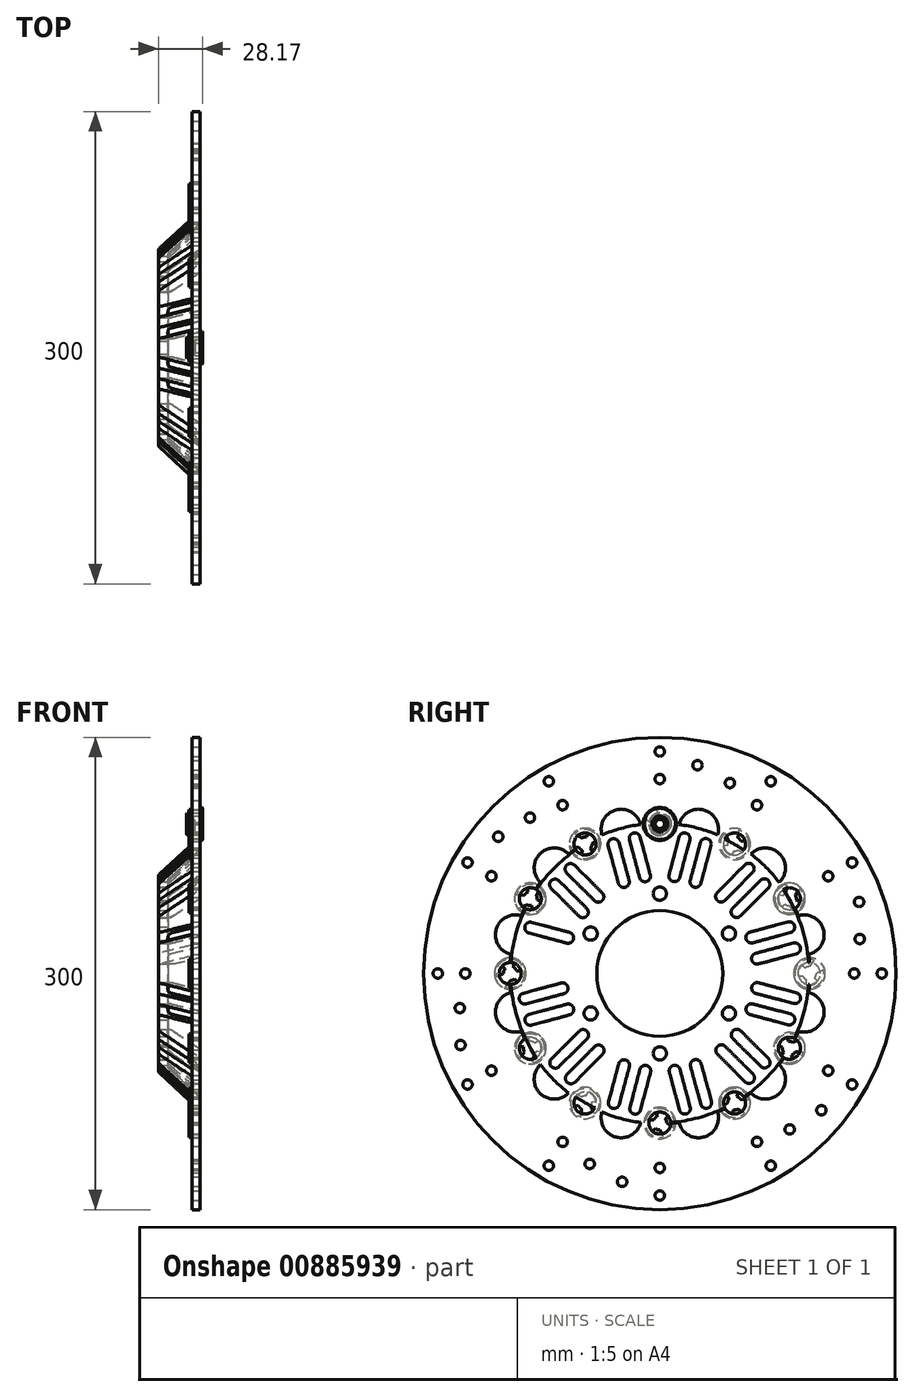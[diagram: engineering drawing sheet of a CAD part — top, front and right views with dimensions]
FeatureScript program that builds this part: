
annotation { "Feature Type Name" : "Feature", "Feature Type Description" : "" }
export const myFeature = defineFeature(function(context is Context, id is Id, definition is map)
    precondition{}
    {
        {
            var Q0;
            Q0=qCreatedBy(makeId("Front.planeOp"),FACE);
            var sketch = newSketch(context, id + "F0", { "sketchPlane" : qUnion([Q0])});
            skLineSegment(sketch, "E0", {"start": v(0, 79.9) * mm, "end": v(0, 150) * mm});
            skLineSegment(sketch, "E1", {"start": v(0, 150) * mm, "end": v(-5.08, 150) * mm});
            skLineSegment(sketch, "E2", {"start": v(-5.08, 150) * mm, "end": v(-5.08, 83.37) * mm});
            skLineSegment(sketch, "E3", {"start": v(-5.72, 81.9) * mm, "end": v(-25.96, 63.1) * mm});
            skLineSegment(sketch, "E4", {"start": v(-26.6, 61.63) * mm, "end": v(-26.6, 0) * mm});
            skLineSegment(sketch, "E5", {"start": v(-5.08, 82.5) * mm, "end": v(-5.08, 0) * mm, "construction": true});
            skLineSegment(sketch, "E6", {"start": v(-26.6, 0) * mm, "end": v(-20.6, 0) * mm});
            skLineSegment(sketch, "E7", {"start": v(-20.6, 0) * mm, "end": v(-20.6, 59.01) * mm});
            skLineSegment(sketch, "E8", {"start": v(-19.96, 60.48) * mm, "end": v(-0.64, 78.44) * mm});
            skPoint(sketch, "E9.visualSharp", {"position": v(-5.08, 82.5) * mm});
            skArc(sketch, "E9.filletArc", {"start": v(-5.72, 81.9) * mm, "mid": v(-5.25, 82.57) * mm, "end": v(-5.08, 83.37) * mm});
            skPoint(sketch, "E10.newPointB", {"position": v(0, 0) * mm});
            skArc(sketch, "E10.filletArc", {"start": v(-0.64, 78.44) * mm, "mid": v(-0.17, 79.1) * mm, "end": v(0, 79.9) * mm});
            skPoint(sketch, "E11.visualSharp", {"position": v(-26.6, 62.5) * mm});
            skArc(sketch, "E11.filletArc", {"start": v(-25.96, 63.1) * mm, "mid": v(-26.43, 62.43) * mm, "end": v(-26.6, 61.63) * mm});
            skPoint(sketch, "E12.visualSharp", {"position": v(-20.6, 59.89) * mm});
            skArc(sketch, "E12.filletArc", {"start": v(-19.96, 60.48) * mm, "mid": v(-20.43, 59.81) * mm, "end": v(-20.6, 59.01) * mm});
            skSolve(sketch);
        }
        {
            var Q0;
            Q0=makeQuery(id+"F0.imprint","IMPRINT",FACE,{"disambiguationData":[TD([[makeQuery(id+"F0.imprint","IMPRINT",EDGE,{"derivedFrom":sQuery(id+"F0.wireOp",EDGE,"E0")}),1.0]])]});
            var Q1;
            Q1=sQuery(id+"F0.wireOp",EDGE,"E6");
            revolve(context, id + "F1", {"surfaceOperationType" : NewSurfaceOperationType.NEW, "entities" : qUnion([Q0]), "axis" : qUnion([Q1]), "revolveType" : RevolveType.FULL});
        }
        {
            var Q0;
            Q0=qCreatedBy(makeId("Right.planeOp"),FACE);
            var sketch = newSketch(context, id + "F2", { "sketchPlane" : qUnion([Q0])});
            skCircle(sketch, "E13", {"center": v(0, 0) * mm, "radius": 39.98 * mm});
            skLineSegment(sketch, "E14", {"start": v(0, 0) * mm, "end": v(0, 50.7) * mm, "construction": true});
            skCircle(sketch, "E15", {"center": v(0, 50.7) * mm, "radius": 4.2 * mm});
            skPoint(sketch, "E16.center", {"position": v(55.17, 0) * mm});
            skLineSegment(sketch, "E17", {"start": v(0, 0) * mm, "end": v(95, 0) * mm, "construction": true});
            skCircle(sketch, "E18", {"center": v(95, 0) * mm, "radius": 7 * mm});
            skCircle(sketch, "E19.1.0", {"center": v(82.27, 47.5) * mm, "radius": 7 * mm});
            skCircle(sketch, "E19.2.0", {"center": v(47.5, 82.27) * mm, "radius": 7 * mm});
            skCircle(sketch, "E19.3.0", {"center": v(0, 95) * mm, "radius": 7 * mm});
            skCircle(sketch, "E19.4.0", {"center": v(-47.5, 82.27) * mm, "radius": 7 * mm});
            skCircle(sketch, "E19.5.0", {"center": v(-82.27, 47.5) * mm, "radius": 7 * mm});
            skCircle(sketch, "E19.6.0", {"center": v(-95, 0) * mm, "radius": 7 * mm});
            skCircle(sketch, "E19.7.0", {"center": v(-82.27, -47.5) * mm, "radius": 7 * mm});
            skCircle(sketch, "E19.8.0", {"center": v(-47.5, -82.27) * mm, "radius": 7 * mm});
            skCircle(sketch, "E19.9.0", {"center": v(0, -95) * mm, "radius": 7 * mm});
            skCircle(sketch, "E19.10.0", {"center": v(47.5, -82.27) * mm, "radius": 7 * mm});
            skCircle(sketch, "E19.11.0", {"center": v(82.27, -47.5) * mm, "radius": 7 * mm});
            skCircle(sketch, "E20", {"center": v(0, 0) * mm, "radius": 87 * mm, "construction": true});
            skLineSegment(sketch, "E21", {"start": v(-84.07, 22.39) * mm, "end": v(0, 0) * mm, "construction": true});
            skLineSegment(sketch, "E22", {"start": v(-84.07, 22.39) * mm, "end": v(-82.26, 29.15) * mm, "construction": true});
            skArc(sketch, "E23", {"start": v(-81.35, 32.53) * mm, "mid": v(-85.64, 30.05) * mm, "end": v(-83.16, 25.77) * mm});
            skCircle(sketch, "E24.0", {"center": v(0, 0) * mm, "radius": 59.01 * mm, "construction": true});
            skLineSegment(sketch, "E25", {"start": v(-82.26, 29.15) * mm, "end": v(-58.24, 22.71) * mm, "construction": true});
            skArc(sketch, "E26", {"start": v(-59.15, 19.33) * mm, "mid": v(-54.86, 21.8) * mm, "end": v(-57.34, 26.1) * mm});
            skLineSegment(sketch, "E27", {"start": v(-81.35, 32.53) * mm, "end": v(-57.34, 26.1) * mm});
            skLineSegment(sketch, "E28", {"start": v(-83.16, 25.77) * mm, "end": v(-59.15, 19.33) * mm});
            skArc(sketch, "E29.MirrorCS", {"start": v(-60.93, 12.64) * mm, "mid": v(-58.44, 8.36) * mm, "end": v(-62.72, 5.87) * mm});
            skLineSegment(sketch, "E30.MirrorCS", {"start": v(-84.97, 19) * mm, "end": v(-60.93, 12.64) * mm});
            skLineSegment(sketch, "E31.MirrorCS", {"start": v(-86.76, 12.23) * mm, "end": v(-62.72, 5.87) * mm});
            skArc(sketch, "E32.MirrorCS", {"start": v(-86.76, 12.23) * mm, "mid": v(-89.24, 16.51) * mm, "end": v(-84.97, 19) * mm});
            skArc(sketch, "E33.1.0", {"start": v(-86.72, -12.5) * mm, "mid": v(-89.2, -16.8) * mm, "end": v(-84.9, -19.27) * mm});
            skLineSegment(sketch, "E33.1.1", {"start": v(-86.72, -12.5) * mm, "end": v(-62.7, -6.07) * mm});
            skArc(sketch, "E33.1.2", {"start": v(-60.89, -12.83) * mm, "mid": v(-58.41, -8.55) * mm, "end": v(-62.7, -6.07) * mm});
            skLineSegment(sketch, "E33.1.3", {"start": v(-84.9, -19.27) * mm, "end": v(-60.89, -12.83) * mm});
            skLineSegment(sketch, "E33.1.4", {"start": v(-83.08, -26.03) * mm, "end": v(-59.09, -19.52) * mm});
            skArc(sketch, "E33.1.5", {"start": v(-81.25, -32.78) * mm, "mid": v(-85.55, -30.32) * mm, "end": v(-83.08, -26.03) * mm});
            skLineSegment(sketch, "E33.1.6", {"start": v(-81.25, -32.78) * mm, "end": v(-57.25, -26.27) * mm});
            skArc(sketch, "E33.1.7", {"start": v(-59.09, -19.52) * mm, "mid": v(-54.8, -21.98) * mm, "end": v(-57.25, -26.27) * mm});
            skArc(sketch, "E33.2.0", {"start": v(-68.85, -54.19) * mm, "mid": v(-68.85, -59.14) * mm, "end": v(-63.9, -59.14) * mm});
            skLineSegment(sketch, "E33.2.1", {"start": v(-68.85, -54.19) * mm, "end": v(-51.26, -36.6) * mm});
            skArc(sketch, "E33.2.2", {"start": v(-46.31, -41.56) * mm, "mid": v(-46.31, -36.6) * mm, "end": v(-51.26, -36.6) * mm});
            skLineSegment(sketch, "E33.2.3", {"start": v(-63.9, -59.14) * mm, "end": v(-46.31, -41.56) * mm});
            skLineSegment(sketch, "E33.2.4", {"start": v(-58.94, -64.08) * mm, "end": v(-41.41, -46.44) * mm});
            skArc(sketch, "E33.2.5", {"start": v(-53.97, -69.02) * mm, "mid": v(-58.92, -69.03) * mm, "end": v(-58.94, -64.08) * mm});
            skLineSegment(sketch, "E33.2.6", {"start": v(-53.97, -69.02) * mm, "end": v(-36.45, -51.38) * mm});
            skArc(sketch, "E33.2.7", {"start": v(-41.41, -46.44) * mm, "mid": v(-36.46, -46.43) * mm, "end": v(-36.45, -51.38) * mm});
            skArc(sketch, "E33.3.0", {"start": v(-32.53, -81.35) * mm, "mid": v(-30.05, -85.64) * mm, "end": v(-25.77, -83.16) * mm});
            skLineSegment(sketch, "E33.3.1", {"start": v(-32.53, -81.35) * mm, "end": v(-26.1, -57.34) * mm});
            skArc(sketch, "E33.3.2", {"start": v(-19.33, -59.15) * mm, "mid": v(-21.8, -54.86) * mm, "end": v(-26.1, -57.34) * mm});
            skLineSegment(sketch, "E33.3.3", {"start": v(-25.77, -83.16) * mm, "end": v(-19.33, -59.15) * mm});
            skLineSegment(sketch, "E33.3.4", {"start": v(-19, -84.97) * mm, "end": v(-12.64, -60.93) * mm});
            skArc(sketch, "E33.3.5", {"start": v(-12.23, -86.76) * mm, "mid": v(-16.51, -89.24) * mm, "end": v(-19, -84.97) * mm});
            skLineSegment(sketch, "E33.3.6", {"start": v(-12.23, -86.76) * mm, "end": v(-5.87, -62.72) * mm});
            skArc(sketch, "E33.3.7", {"start": v(-12.64, -60.93) * mm, "mid": v(-8.36, -58.44) * mm, "end": v(-5.87, -62.72) * mm});
            skArc(sketch, "E33.4.0", {"start": v(12.5, -86.72) * mm, "mid": v(16.8, -89.2) * mm, "end": v(19.27, -84.9) * mm});
            skLineSegment(sketch, "E33.4.1", {"start": v(12.5, -86.72) * mm, "end": v(6.07, -62.7) * mm});
            skArc(sketch, "E33.4.2", {"start": v(12.83, -60.89) * mm, "mid": v(8.55, -58.41) * mm, "end": v(6.07, -62.7) * mm});
            skLineSegment(sketch, "E33.4.3", {"start": v(19.27, -84.9) * mm, "end": v(12.83, -60.89) * mm});
            skLineSegment(sketch, "E33.4.4", {"start": v(26.03, -83.08) * mm, "end": v(19.52, -59.09) * mm});
            skArc(sketch, "E33.4.5", {"start": v(32.78, -81.25) * mm, "mid": v(30.32, -85.55) * mm, "end": v(26.03, -83.08) * mm});
            skLineSegment(sketch, "E33.4.6", {"start": v(32.78, -81.25) * mm, "end": v(26.27, -57.25) * mm});
            skArc(sketch, "E33.4.7", {"start": v(19.52, -59.09) * mm, "mid": v(21.98, -54.8) * mm, "end": v(26.27, -57.25) * mm});
            skArc(sketch, "E33.5.0", {"start": v(54.19, -68.85) * mm, "mid": v(59.14, -68.85) * mm, "end": v(59.14, -63.9) * mm});
            skLineSegment(sketch, "E33.5.1", {"start": v(54.19, -68.85) * mm, "end": v(36.6, -51.26) * mm});
            skArc(sketch, "E33.5.2", {"start": v(41.56, -46.31) * mm, "mid": v(36.6, -46.31) * mm, "end": v(36.6, -51.26) * mm});
            skLineSegment(sketch, "E33.5.3", {"start": v(59.14, -63.9) * mm, "end": v(41.56, -46.31) * mm});
            skLineSegment(sketch, "E33.5.4", {"start": v(64.08, -58.94) * mm, "end": v(46.44, -41.41) * mm});
            skArc(sketch, "E33.5.5", {"start": v(69.02, -53.97) * mm, "mid": v(69.03, -58.92) * mm, "end": v(64.08, -58.94) * mm});
            skLineSegment(sketch, "E33.5.6", {"start": v(69.02, -53.97) * mm, "end": v(51.38, -36.45) * mm});
            skArc(sketch, "E33.5.7", {"start": v(46.44, -41.41) * mm, "mid": v(46.43, -36.46) * mm, "end": v(51.38, -36.45) * mm});
            skArc(sketch, "E33.6.0", {"start": v(81.35, -32.53) * mm, "mid": v(85.64, -30.05) * mm, "end": v(83.16, -25.77) * mm});
            skLineSegment(sketch, "E33.6.1", {"start": v(81.35, -32.53) * mm, "end": v(57.34, -26.1) * mm});
            skArc(sketch, "E33.6.2", {"start": v(59.15, -19.33) * mm, "mid": v(54.86, -21.8) * mm, "end": v(57.34, -26.1) * mm});
            skLineSegment(sketch, "E33.6.3", {"start": v(83.16, -25.77) * mm, "end": v(59.15, -19.33) * mm});
            skLineSegment(sketch, "E33.6.4", {"start": v(84.97, -19) * mm, "end": v(60.93, -12.64) * mm});
            skArc(sketch, "E33.6.5", {"start": v(86.76, -12.23) * mm, "mid": v(89.24, -16.51) * mm, "end": v(84.97, -19) * mm});
            skLineSegment(sketch, "E33.6.6", {"start": v(86.76, -12.23) * mm, "end": v(62.72, -5.87) * mm});
            skArc(sketch, "E33.6.7", {"start": v(60.93, -12.64) * mm, "mid": v(58.44, -8.36) * mm, "end": v(62.72, -5.87) * mm});
            skArc(sketch, "E33.7.0", {"start": v(86.72, 12.5) * mm, "mid": v(89.2, 16.8) * mm, "end": v(84.9, 19.27) * mm});
            skLineSegment(sketch, "E33.7.1", {"start": v(86.72, 12.5) * mm, "end": v(62.7, 6.07) * mm});
            skArc(sketch, "E33.7.2", {"start": v(60.89, 12.83) * mm, "mid": v(58.41, 8.55) * mm, "end": v(62.7, 6.07) * mm});
            skLineSegment(sketch, "E33.7.3", {"start": v(84.9, 19.27) * mm, "end": v(60.89, 12.83) * mm});
            skLineSegment(sketch, "E33.7.4", {"start": v(83.08, 26.03) * mm, "end": v(59.09, 19.52) * mm});
            skArc(sketch, "E33.7.5", {"start": v(81.25, 32.78) * mm, "mid": v(85.55, 30.32) * mm, "end": v(83.08, 26.03) * mm});
            skLineSegment(sketch, "E33.7.6", {"start": v(81.25, 32.78) * mm, "end": v(57.25, 26.27) * mm});
            skArc(sketch, "E33.7.7", {"start": v(59.09, 19.52) * mm, "mid": v(54.8, 21.98) * mm, "end": v(57.25, 26.27) * mm});
            skArc(sketch, "E33.8.0", {"start": v(68.85, 54.19) * mm, "mid": v(68.85, 59.14) * mm, "end": v(63.9, 59.14) * mm});
            skLineSegment(sketch, "E33.8.1", {"start": v(68.85, 54.19) * mm, "end": v(51.26, 36.6) * mm});
            skArc(sketch, "E33.8.2", {"start": v(46.31, 41.56) * mm, "mid": v(46.31, 36.6) * mm, "end": v(51.26, 36.6) * mm});
            skLineSegment(sketch, "E33.8.3", {"start": v(63.9, 59.14) * mm, "end": v(46.31, 41.56) * mm});
            skLineSegment(sketch, "E33.8.4", {"start": v(58.94, 64.08) * mm, "end": v(41.41, 46.44) * mm});
            skArc(sketch, "E33.8.5", {"start": v(53.97, 69.02) * mm, "mid": v(58.92, 69.03) * mm, "end": v(58.94, 64.08) * mm});
            skLineSegment(sketch, "E33.8.6", {"start": v(53.97, 69.02) * mm, "end": v(36.45, 51.38) * mm});
            skArc(sketch, "E33.8.7", {"start": v(41.41, 46.44) * mm, "mid": v(36.46, 46.43) * mm, "end": v(36.45, 51.38) * mm});
            skArc(sketch, "E33.9.0", {"start": v(32.53, 81.35) * mm, "mid": v(30.05, 85.64) * mm, "end": v(25.77, 83.16) * mm});
            skLineSegment(sketch, "E33.9.1", {"start": v(32.53, 81.35) * mm, "end": v(26.1, 57.34) * mm});
            skArc(sketch, "E33.9.2", {"start": v(19.33, 59.15) * mm, "mid": v(21.8, 54.86) * mm, "end": v(26.1, 57.34) * mm});
            skLineSegment(sketch, "E33.9.3", {"start": v(25.77, 83.16) * mm, "end": v(19.33, 59.15) * mm});
            skLineSegment(sketch, "E33.9.4", {"start": v(19, 84.97) * mm, "end": v(12.64, 60.93) * mm});
            skArc(sketch, "E33.9.5", {"start": v(12.23, 86.76) * mm, "mid": v(16.51, 89.24) * mm, "end": v(19, 84.97) * mm});
            skLineSegment(sketch, "E33.9.6", {"start": v(12.23, 86.76) * mm, "end": v(5.87, 62.72) * mm});
            skArc(sketch, "E33.9.7", {"start": v(12.64, 60.93) * mm, "mid": v(8.36, 58.44) * mm, "end": v(5.87, 62.72) * mm});
            skArc(sketch, "E33.10.0", {"start": v(-12.5, 86.72) * mm, "mid": v(-16.8, 89.2) * mm, "end": v(-19.27, 84.9) * mm});
            skLineSegment(sketch, "E33.10.1", {"start": v(-12.5, 86.72) * mm, "end": v(-6.07, 62.7) * mm});
            skArc(sketch, "E33.10.2", {"start": v(-12.83, 60.89) * mm, "mid": v(-8.55, 58.41) * mm, "end": v(-6.07, 62.7) * mm});
            skLineSegment(sketch, "E33.10.3", {"start": v(-19.27, 84.9) * mm, "end": v(-12.83, 60.89) * mm});
            skLineSegment(sketch, "E33.10.4", {"start": v(-26.03, 83.08) * mm, "end": v(-19.52, 59.09) * mm});
            skArc(sketch, "E33.10.5", {"start": v(-32.78, 81.25) * mm, "mid": v(-30.32, 85.55) * mm, "end": v(-26.03, 83.08) * mm});
            skLineSegment(sketch, "E33.10.6", {"start": v(-32.78, 81.25) * mm, "end": v(-26.27, 57.25) * mm});
            skArc(sketch, "E33.10.7", {"start": v(-19.52, 59.09) * mm, "mid": v(-21.98, 54.8) * mm, "end": v(-26.27, 57.25) * mm});
            skArc(sketch, "E33.11.0", {"start": v(-54.19, 68.85) * mm, "mid": v(-59.14, 68.85) * mm, "end": v(-59.14, 63.9) * mm});
            skLineSegment(sketch, "E33.11.1", {"start": v(-54.19, 68.85) * mm, "end": v(-36.6, 51.26) * mm});
            skArc(sketch, "E33.11.2", {"start": v(-41.56, 46.31) * mm, "mid": v(-36.6, 46.31) * mm, "end": v(-36.6, 51.26) * mm});
            skLineSegment(sketch, "E33.11.3", {"start": v(-59.14, 63.9) * mm, "end": v(-41.56, 46.31) * mm});
            skLineSegment(sketch, "E33.11.4", {"start": v(-64.08, 58.94) * mm, "end": v(-46.44, 41.41) * mm});
            skArc(sketch, "E33.11.5", {"start": v(-69.02, 53.97) * mm, "mid": v(-69.03, 58.92) * mm, "end": v(-64.08, 58.94) * mm});
            skLineSegment(sketch, "E33.11.6", {"start": v(-69.02, 53.97) * mm, "end": v(-51.38, 36.45) * mm});
            skArc(sketch, "E33.11.7", {"start": v(-46.44, 41.41) * mm, "mid": v(-46.43, 36.46) * mm, "end": v(-51.38, 36.45) * mm});
            skCircle(sketch, "E34.1.0", {"center": v(-43.9, 25.35) * mm, "radius": 4.2 * mm});
            skCircle(sketch, "E34.2.0", {"center": v(-43.9, -25.35) * mm, "radius": 4.2 * mm});
            skCircle(sketch, "E34.3.0", {"center": v(0, -50.7) * mm, "radius": 4.2 * mm});
            skCircle(sketch, "E34.4.0", {"center": v(43.9, -25.35) * mm, "radius": 4.2 * mm});
            skCircle(sketch, "E34.5.0", {"center": v(43.9, 25.35) * mm, "radius": 4.2 * mm});
            skCircle(sketch, "E35", {"center": v(0, 0) * mm, "radius": 95.4 * mm});
            skCircle(sketch, "E36", {"center": v(0, 0) * mm, "radius": 94.8 * mm});
            skLineSegment(sketch, "E37", {"start": v(-95, 0) * mm, "end": v(-123.5, 0) * mm, "construction": true});
            skCircle(sketch, "E38", {"center": v(-123.5, 0) * mm, "radius": 3 * mm});
            skLineSegment(sketch, "E39", {"start": v(-95, 0) * mm, "end": v(-141, 0) * mm, "construction": true});
            skCircle(sketch, "E40", {"center": v(-141, 0) * mm, "radius": 3 * mm});
            skCircle(sketch, "E41.1.0", {"center": v(-122.1, -70.5) * mm, "radius": 3 * mm});
            skCircle(sketch, "E41.1.1", {"center": v(-106.95, -61.75) * mm, "radius": 3 * mm});
            skCircle(sketch, "E41.2.0", {"center": v(-70.5, -122.1) * mm, "radius": 3 * mm});
            skCircle(sketch, "E41.2.1", {"center": v(-61.75, -106.95) * mm, "radius": 3 * mm});
            skCircle(sketch, "E41.3.0", {"center": v(0, -141) * mm, "radius": 3 * mm});
            skCircle(sketch, "E41.3.1", {"center": v(0, -123.5) * mm, "radius": 3 * mm});
            skCircle(sketch, "E41.4.0", {"center": v(70.5, -122.1) * mm, "radius": 3 * mm});
            skCircle(sketch, "E41.4.1", {"center": v(61.75, -106.95) * mm, "radius": 3 * mm});
            skCircle(sketch, "E41.5.0", {"center": v(122.1, -70.5) * mm, "radius": 3 * mm});
            skCircle(sketch, "E41.5.1", {"center": v(106.95, -61.75) * mm, "radius": 3 * mm});
            skCircle(sketch, "E41.6.0", {"center": v(141, 0) * mm, "radius": 3 * mm});
            skCircle(sketch, "E41.6.1", {"center": v(123.5, 0) * mm, "radius": 3 * mm});
            skCircle(sketch, "E41.7.0", {"center": v(122.1, 70.5) * mm, "radius": 3 * mm});
            skCircle(sketch, "E41.7.1", {"center": v(106.95, 61.75) * mm, "radius": 3 * mm});
            skCircle(sketch, "E41.8.0", {"center": v(70.5, 122.1) * mm, "radius": 3 * mm});
            skCircle(sketch, "E41.8.1", {"center": v(61.75, 106.95) * mm, "radius": 3 * mm});
            skCircle(sketch, "E41.9.0", {"center": v(0, 141) * mm, "radius": 3 * mm});
            skCircle(sketch, "E41.9.1", {"center": v(0, 123.5) * mm, "radius": 3 * mm});
            skCircle(sketch, "E41.10.0", {"center": v(-70.5, 122.1) * mm, "radius": 3 * mm});
            skCircle(sketch, "E41.10.1", {"center": v(-61.75, 106.95) * mm, "radius": 3 * mm});
            skCircle(sketch, "E41.11.0", {"center": v(-122.1, 70.5) * mm, "radius": 3 * mm});
            skCircle(sketch, "E41.11.1", {"center": v(-106.95, 61.75) * mm, "radius": 3 * mm});
            skLineSegment(sketch, "E42", {"start": v(-141, 0) * mm, "end": v(-106.95, -61.75) * mm, "construction": true});
            skPoint(sketch, "E43", {"position": v(-122.85, -32.92) * mm});
            skLineSegment(sketch, "E44", {"start": v(-123.5, 0) * mm, "end": v(-122.1, -70.5) * mm, "construction": true});
            skCircle(sketch, "E45", {"center": v(-122.85, -32.92) * mm, "radius": 11.75 * mm, "construction": true});
            skPoint(sketch, "E46", {"position": v(-123.08, -21.17) * mm});
            skPoint(sketch, "E47", {"position": v(-122.62, -44.67) * mm});
            skLineSegment(sketch, "E48", {"start": v(-123.08, -21.17) * mm, "end": v(-127, -21.93) * mm, "construction": true});
            skLineSegment(sketch, "E49", {"start": v(-122.62, -44.67) * mm, "end": v(-126.55, -45.42) * mm, "construction": true});
            skCircle(sketch, "E50", {"center": v(-127, -21.93) * mm, "radius": 3 * mm});
            skCircle(sketch, "E51", {"center": v(-126.55, -45.42) * mm, "radius": 3 * mm});
            skCircle(sketch, "E52.MirrorC", {"center": v(-127, 21.93) * mm, "radius": 3 * mm});
            skCircle(sketch, "E53.MirrorC", {"center": v(-126.55, 45.42) * mm, "radius": 3 * mm});
            skCircle(sketch, "E54.1.0", {"center": v(-102.61, -86.88) * mm, "radius": 3 * mm});
            skCircle(sketch, "E54.1.1", {"center": v(-82.5, -99.03) * mm, "radius": 3 * mm});
            skCircle(sketch, "E54.1.2", {"center": v(-44.51, -120.96) * mm, "radius": 3 * mm});
            skCircle(sketch, "E54.1.3", {"center": v(-23.93, -132.3) * mm, "radius": 3 * mm});
            skCircle(sketch, "E54.2.0", {"center": v(23.93, -132.3) * mm, "radius": 3 * mm});
            skCircle(sketch, "E54.2.1", {"center": v(44.51, -120.96) * mm, "radius": 3 * mm});
            skCircle(sketch, "E54.2.2", {"center": v(82.5, -99.03) * mm, "radius": 3 * mm});
            skCircle(sketch, "E54.2.3", {"center": v(102.61, -86.88) * mm, "radius": 3 * mm});
            skCircle(sketch, "E54.3.0", {"center": v(126.55, -45.42) * mm, "radius": 3 * mm});
            skCircle(sketch, "E54.3.1", {"center": v(127, -21.93) * mm, "radius": 3 * mm});
            skCircle(sketch, "E54.3.2", {"center": v(127, 21.93) * mm, "radius": 3 * mm});
            skCircle(sketch, "E54.3.3", {"center": v(126.55, 45.42) * mm, "radius": 3 * mm});
            skCircle(sketch, "E54.4.0", {"center": v(102.61, 86.88) * mm, "radius": 3 * mm});
            skCircle(sketch, "E54.4.1", {"center": v(82.5, 99.03) * mm, "radius": 3 * mm});
            skCircle(sketch, "E54.4.2", {"center": v(44.51, 120.96) * mm, "radius": 3 * mm});
            skCircle(sketch, "E54.4.3", {"center": v(23.93, 132.3) * mm, "radius": 3 * mm});
            skCircle(sketch, "E54.5.0", {"center": v(-23.93, 132.3) * mm, "radius": 3 * mm});
            skCircle(sketch, "E54.5.1", {"center": v(-44.51, 120.96) * mm, "radius": 3 * mm});
            skCircle(sketch, "E54.5.2", {"center": v(-82.5, 99.03) * mm, "radius": 3 * mm});
            skCircle(sketch, "E54.5.3", {"center": v(-102.61, 86.88) * mm, "radius": 3 * mm});
            skLineSegment(sketch, "E55", {"start": v(0, 0) * mm, "end": v(67.46, 67.46) * mm, "construction": true});
            skArc(sketch, "E56.trimOffspring", {"start": v(75.84, 57.88) * mm, "mid": v(76.07, 76.07) * mm, "end": v(57.88, 75.83) * mm});
            skArc(sketch, "E57.1.0", {"start": v(36.74, 88.04) * mm, "mid": v(27.85, 103.91) * mm, "end": v(12.21, 94.62) * mm});
            skArc(sketch, "E57.2.0", {"start": v(-12.2, 94.62) * mm, "mid": v(-27.84, 103.91) * mm, "end": v(-36.73, 88.04) * mm});
            skArc(sketch, "E57.3.0", {"start": v(-57.88, 75.84) * mm, "mid": v(-76.07, 76.07) * mm, "end": v(-75.83, 57.88) * mm});
            skArc(sketch, "E57.4.0", {"start": v(-88.04, 36.74) * mm, "mid": v(-103.91, 27.85) * mm, "end": v(-94.62, 12.21) * mm});
            skArc(sketch, "E57.5.0", {"start": v(-94.62, -12.2) * mm, "mid": v(-103.91, -27.84) * mm, "end": v(-88.04, -36.73) * mm});
            skArc(sketch, "E57.6.0", {"start": v(-75.84, -57.88) * mm, "mid": v(-76.07, -76.07) * mm, "end": v(-57.88, -75.83) * mm});
            skArc(sketch, "E57.7.0", {"start": v(-36.74, -88.04) * mm, "mid": v(-27.85, -103.91) * mm, "end": v(-12.21, -94.62) * mm});
            skArc(sketch, "E57.8.0", {"start": v(12.2, -94.62) * mm, "mid": v(27.84, -103.91) * mm, "end": v(36.73, -88.04) * mm});
            skArc(sketch, "E57.9.0", {"start": v(57.88, -75.84) * mm, "mid": v(76.07, -76.07) * mm, "end": v(75.83, -57.88) * mm});
            skArc(sketch, "E57.10.0", {"start": v(88.04, -36.74) * mm, "mid": v(103.91, -27.85) * mm, "end": v(94.62, -12.21) * mm});
            skArc(sketch, "E57.11.0", {"start": v(94.62, 12.2) * mm, "mid": v(103.91, 27.84) * mm, "end": v(88.04, 36.73) * mm});
            skSolve(sketch);
        }
        {
            var Q0;
            Q0=makeQuery(id+"F2.imprint","IMPRINT",FACE,{"disambiguationData":[TD([[makeQuery(id+"F2.imprint","IMPRINT",EDGE,{"derivedFrom":sQuery(id+"F2.wireOp",EDGE,"E33.11.0")}),1.0]])]});
            var Q1;
            Q1=makeQuery(id+"F2.imprint","IMPRINT",FACE,{"disambiguationData":[TD([[makeQuery(id+"F2.imprint","IMPRINT",EDGE,{"derivedFrom":sQuery(id+"F2.wireOp",EDGE,"E33.11.4")}),-1.0]])]});
            var Q2;
            Q2=makeQuery(id+"F2.imprint","IMPRINT",FACE,{"disambiguationData":[TD([[makeQuery(id+"F2.imprint","IMPRINT",EDGE,{"derivedFrom":sQuery(id+"F2.wireOp",EDGE,"E34.1.0")}),1.0]])]});
            var Q3;
            Q3=makeQuery(id+"F2.imprint","IMPRINT",FACE,{"disambiguationData":[TD([[makeQuery(id+"F2.imprint","IMPRINT",EDGE,{"derivedFrom":sQuery(id+"F2.wireOp",EDGE,"E15")}),1.0]])]});
            var Q4;
            Q4=makeQuery(id+"F2.imprint","IMPRINT",FACE,{"disambiguationData":[TD([[makeQuery(id+"F2.imprint","IMPRINT",EDGE,{"derivedFrom":sQuery(id+"F2.wireOp",EDGE,"E33.10.4")}),-1.0]])]});
            var Q5;
            Q5=makeQuery(id+"F2.imprint","IMPRINT",FACE,{"disambiguationData":[TD([[makeQuery(id+"F2.imprint","IMPRINT",EDGE,{"derivedFrom":sQuery(id+"F2.wireOp",EDGE,"E33.10.0")}),1.0]])]});
            var Q6;
            {var subQ0=sQuery(id+"F2.wireOp",EDGE,"E36");var subQ1=sQuery(id+"F2.wireOp",EDGE,"E19.4.0");var subQ2=makeQuery(id+"F2.imprint","INTERSECT",VERTEX,{"disambiguationData":[OD(0.0)],"derivedFrom":[subQ1,subQ0]});Q6=makeQuery(id+"F2.imprint","IMPRINT",FACE,{"disambiguationData":[TD([[makeQuery(id+"F2.imprint","IMPRINT",EDGE,{"disambiguationData":[TD([[subQ2,1.0]])],"derivedFrom":subQ1}),1.0]])]});}
            var Q7;
            {var subQ0=sQuery(id+"F2.wireOp",EDGE,"E35");var subQ4=makeQuery(id+"F2.imprint","IMPRINT",VERTEX,{"derivedFrom":subQ0});Q7=makeQuery(id+"F2.imprint","IMPRINT",FACE,{"disambiguationData":[TD([[makeQuery(id+"F2.imprint","IMPRINT",EDGE,{"disambiguationData":[TD([[subQ4,1.0]])],"derivedFrom":subQ0}),-1.0]])]});}
            var Q8;
            {var subQ0=sQuery(id+"F2.wireOp",EDGE,"E35");var subQ1=sQuery(id+"F2.wireOp",EDGE,"E19.1.0");var subQ2=makeQuery(id+"F2.imprint","INTERSECT",VERTEX,{"disambiguationData":[OD(0.0)],"derivedFrom":[subQ1,subQ0]});Q8=makeQuery(id+"F2.imprint","IMPRINT",FACE,{"disambiguationData":[TD([[makeQuery(id+"F2.imprint","IMPRINT",EDGE,{"disambiguationData":[TD([[subQ2,-1.0]])],"derivedFrom":subQ1}),1.0]])]});}
            var Q9;
            {var subQ0=sQuery(id+"F2.wireOp",EDGE,"E35");var subQ1=sQuery(id+"F2.wireOp",EDGE,"E19.2.0");var subQ2=makeQuery(id+"F2.imprint","INTERSECT",VERTEX,{"disambiguationData":[OD(0.0)],"derivedFrom":[subQ1,subQ0]});Q9=makeQuery(id+"F2.imprint","IMPRINT",FACE,{"disambiguationData":[TD([[makeQuery(id+"F2.imprint","IMPRINT",EDGE,{"disambiguationData":[TD([[subQ2,-1.0]])],"derivedFrom":subQ1}),1.0]])]});}
            var Q10;
            {var subQ0=sQuery(id+"F2.wireOp",EDGE,"E35");var subQ1=sQuery(id+"F2.wireOp",EDGE,"E19.3.0");var subQ2=makeQuery(id+"F2.imprint","INTERSECT",VERTEX,{"disambiguationData":[OD(0.0)],"derivedFrom":[subQ1,subQ0]});Q10=makeQuery(id+"F2.imprint","IMPRINT",FACE,{"disambiguationData":[TD([[makeQuery(id+"F2.imprint","IMPRINT",EDGE,{"disambiguationData":[TD([[subQ2,-1.0]])],"derivedFrom":subQ1}),1.0]])]});}
            var Q11;
            {var subQ0=sQuery(id+"F2.wireOp",EDGE,"E35");var subQ1=sQuery(id+"F2.wireOp",EDGE,"E19.4.0");var subQ2=makeQuery(id+"F2.imprint","INTERSECT",VERTEX,{"disambiguationData":[OD(0.0)],"derivedFrom":[subQ1,subQ0]});Q11=makeQuery(id+"F2.imprint","IMPRINT",FACE,{"disambiguationData":[TD([[makeQuery(id+"F2.imprint","IMPRINT",EDGE,{"disambiguationData":[TD([[subQ2,-1.0]])],"derivedFrom":subQ1}),1.0]])]});}
            var Q12;
            {var subQ0=sQuery(id+"F2.wireOp",EDGE,"E35");var subQ1=sQuery(id+"F2.wireOp",EDGE,"E19.5.0");var subQ2=makeQuery(id+"F2.imprint","INTERSECT",VERTEX,{"disambiguationData":[OD(0.0)],"derivedFrom":[subQ1,subQ0]});Q12=makeQuery(id+"F2.imprint","IMPRINT",FACE,{"disambiguationData":[TD([[makeQuery(id+"F2.imprint","IMPRINT",EDGE,{"disambiguationData":[TD([[subQ2,-1.0]])],"derivedFrom":subQ1}),1.0]])]});}
            var Q13;
            {var subQ0=sQuery(id+"F2.wireOp",EDGE,"E35");var subQ1=sQuery(id+"F2.wireOp",EDGE,"E19.6.0");var subQ2=makeQuery(id+"F2.imprint","INTERSECT",VERTEX,{"disambiguationData":[OD(0.0)],"derivedFrom":[subQ1,subQ0]});Q13=makeQuery(id+"F2.imprint","IMPRINT",FACE,{"disambiguationData":[TD([[makeQuery(id+"F2.imprint","IMPRINT",EDGE,{"disambiguationData":[TD([[subQ2,1.0]])],"derivedFrom":subQ1}),1.0]])]});}
            var Q14;
            {var subQ0=sQuery(id+"F2.wireOp",EDGE,"E35");var subQ1=sQuery(id+"F2.wireOp",EDGE,"E19.7.0");var subQ2=makeQuery(id+"F2.imprint","INTERSECT",VERTEX,{"disambiguationData":[OD(0.0)],"derivedFrom":[subQ1,subQ0]});Q14=makeQuery(id+"F2.imprint","IMPRINT",FACE,{"disambiguationData":[TD([[makeQuery(id+"F2.imprint","IMPRINT",EDGE,{"disambiguationData":[TD([[subQ2,1.0]])],"derivedFrom":subQ1}),1.0]])]});}
            var Q15;
            {var subQ0=sQuery(id+"F2.wireOp",EDGE,"E35");var subQ1=sQuery(id+"F2.wireOp",EDGE,"E19.8.0");var subQ2=makeQuery(id+"F2.imprint","INTERSECT",VERTEX,{"disambiguationData":[OD(0.0)],"derivedFrom":[subQ1,subQ0]});Q15=makeQuery(id+"F2.imprint","IMPRINT",FACE,{"disambiguationData":[TD([[makeQuery(id+"F2.imprint","IMPRINT",EDGE,{"disambiguationData":[TD([[subQ2,1.0]])],"derivedFrom":subQ1}),1.0]])]});}
            var Q16;
            {var subQ0=sQuery(id+"F2.wireOp",EDGE,"E35");var subQ1=sQuery(id+"F2.wireOp",EDGE,"E19.9.0");var subQ2=makeQuery(id+"F2.imprint","INTERSECT",VERTEX,{"disambiguationData":[OD(0.0)],"derivedFrom":[subQ1,subQ0]});Q16=makeQuery(id+"F2.imprint","IMPRINT",FACE,{"disambiguationData":[TD([[makeQuery(id+"F2.imprint","IMPRINT",EDGE,{"disambiguationData":[TD([[subQ2,1.0]])],"derivedFrom":subQ1}),1.0]])]});}
            var Q17;
            {var subQ0=sQuery(id+"F2.wireOp",EDGE,"E35");var subQ1=sQuery(id+"F2.wireOp",EDGE,"E19.10.0");var subQ2=makeQuery(id+"F2.imprint","INTERSECT",VERTEX,{"disambiguationData":[OD(0.0)],"derivedFrom":[subQ1,subQ0]});Q17=makeQuery(id+"F2.imprint","IMPRINT",FACE,{"disambiguationData":[TD([[makeQuery(id+"F2.imprint","IMPRINT",EDGE,{"disambiguationData":[TD([[subQ2,1.0]])],"derivedFrom":subQ1}),1.0]])]});}
            var Q18;
            {var subQ0=sQuery(id+"F2.wireOp",EDGE,"E35");var subQ1=sQuery(id+"F2.wireOp",EDGE,"E19.11.0");var subQ2=makeQuery(id+"F2.imprint","INTERSECT",VERTEX,{"disambiguationData":[OD(0.0)],"derivedFrom":[subQ1,subQ0]});Q18=makeQuery(id+"F2.imprint","IMPRINT",FACE,{"disambiguationData":[TD([[makeQuery(id+"F2.imprint","IMPRINT",EDGE,{"disambiguationData":[TD([[subQ2,1.0]])],"derivedFrom":subQ1}),1.0]])]});}
            var Q19;
            {var subQ0=sQuery(id+"F2.wireOp",EDGE,"E35");var subQ1=sQuery(id+"F2.wireOp",EDGE,"E18");var subQ2=makeQuery(id+"F2.imprint","INTERSECT",VERTEX,{"disambiguationData":[OD(0.0)],"derivedFrom":[subQ1,subQ0]});Q19=makeQuery(id+"F2.imprint","IMPRINT",FACE,{"disambiguationData":[TD([[makeQuery(id+"F2.imprint","IMPRINT",EDGE,{"disambiguationData":[TD([[subQ2,-1.0]])],"derivedFrom":subQ1}),-1.0]])]});}
            var Q20;
            {var subQ0=sQuery(id+"F2.wireOp",EDGE,"E35");var subQ1=sQuery(id+"F2.wireOp",EDGE,"E18");var subQ2=makeQuery(id+"F2.imprint","INTERSECT",VERTEX,{"disambiguationData":[OD(1.0)],"derivedFrom":[subQ1,subQ0]});Q20=makeQuery(id+"F2.imprint","IMPRINT",FACE,{"disambiguationData":[TD([[makeQuery(id+"F2.imprint","IMPRINT",EDGE,{"disambiguationData":[TD([[subQ2,1.0]])],"derivedFrom":subQ1}),-1.0]])]});}
            var Q21;
            {var subQ0=sQuery(id+"F2.wireOp",EDGE,"E35");var subQ1=sQuery(id+"F2.wireOp",EDGE,"E19.1.0");var subQ2=makeQuery(id+"F2.imprint","INTERSECT",VERTEX,{"disambiguationData":[OD(1.0)],"derivedFrom":[subQ1,subQ0]});Q21=makeQuery(id+"F2.imprint","IMPRINT",FACE,{"disambiguationData":[TD([[makeQuery(id+"F2.imprint","IMPRINT",EDGE,{"disambiguationData":[TD([[subQ2,-1.0]])],"derivedFrom":subQ1}),-1.0]])]});}
            var Q22;
            {var subQ0=sQuery(id+"F2.wireOp",EDGE,"E35");var subQ1=sQuery(id+"F2.wireOp",EDGE,"E19.2.0");var subQ2=makeQuery(id+"F2.imprint","INTERSECT",VERTEX,{"disambiguationData":[OD(1.0)],"derivedFrom":[subQ1,subQ0]});Q22=makeQuery(id+"F2.imprint","IMPRINT",FACE,{"disambiguationData":[TD([[makeQuery(id+"F2.imprint","IMPRINT",EDGE,{"disambiguationData":[TD([[subQ2,-1.0]])],"derivedFrom":subQ1}),-1.0]])]});}
            var Q23;
            {var subQ0=sQuery(id+"F2.wireOp",EDGE,"E35");var subQ1=sQuery(id+"F2.wireOp",EDGE,"E19.3.0");var subQ2=makeQuery(id+"F2.imprint","INTERSECT",VERTEX,{"disambiguationData":[OD(1.0)],"derivedFrom":[subQ1,subQ0]});Q23=makeQuery(id+"F2.imprint","IMPRINT",FACE,{"disambiguationData":[TD([[makeQuery(id+"F2.imprint","IMPRINT",EDGE,{"disambiguationData":[TD([[subQ2,-1.0]])],"derivedFrom":subQ1}),-1.0]])]});}
            var Q24;
            {var subQ0=sQuery(id+"F2.wireOp",EDGE,"E35");var subQ1=sQuery(id+"F2.wireOp",EDGE,"E19.4.0");var subQ2=makeQuery(id+"F2.imprint","INTERSECT",VERTEX,{"disambiguationData":[OD(1.0)],"derivedFrom":[subQ1,subQ0]});Q24=makeQuery(id+"F2.imprint","IMPRINT",FACE,{"disambiguationData":[TD([[makeQuery(id+"F2.imprint","IMPRINT",EDGE,{"disambiguationData":[TD([[subQ2,-1.0]])],"derivedFrom":subQ1}),-1.0]])]});}
            var Q25;
            {var subQ0=sQuery(id+"F2.wireOp",EDGE,"E35");var subQ1=sQuery(id+"F2.wireOp",EDGE,"E19.5.0");var subQ2=makeQuery(id+"F2.imprint","INTERSECT",VERTEX,{"disambiguationData":[OD(1.0)],"derivedFrom":[subQ1,subQ0]});Q25=makeQuery(id+"F2.imprint","IMPRINT",FACE,{"disambiguationData":[TD([[makeQuery(id+"F2.imprint","IMPRINT",EDGE,{"disambiguationData":[TD([[subQ2,-1.0]])],"derivedFrom":subQ1}),-1.0]])]});}
            var Q26;
            {var subQ0=sQuery(id+"F2.wireOp",EDGE,"E35");var subQ1=sQuery(id+"F2.wireOp",EDGE,"E19.6.0");var subQ2=makeQuery(id+"F2.imprint","INTERSECT",VERTEX,{"disambiguationData":[OD(0.0)],"derivedFrom":[subQ1,subQ0]});Q26=makeQuery(id+"F2.imprint","IMPRINT",FACE,{"disambiguationData":[TD([[makeQuery(id+"F2.imprint","IMPRINT",EDGE,{"disambiguationData":[TD([[subQ2,-1.0]])],"derivedFrom":subQ1}),-1.0]])]});}
            var Q27;
            {var subQ0=sQuery(id+"F2.wireOp",EDGE,"E35");var subQ1=sQuery(id+"F2.wireOp",EDGE,"E19.7.0");var subQ2=makeQuery(id+"F2.imprint","INTERSECT",VERTEX,{"disambiguationData":[OD(0.0)],"derivedFrom":[subQ1,subQ0]});Q27=makeQuery(id+"F2.imprint","IMPRINT",FACE,{"disambiguationData":[TD([[makeQuery(id+"F2.imprint","IMPRINT",EDGE,{"disambiguationData":[TD([[subQ2,-1.0]])],"derivedFrom":subQ1}),-1.0]])]});}
            var Q28;
            {var subQ0=sQuery(id+"F2.wireOp",EDGE,"E35");var subQ1=sQuery(id+"F2.wireOp",EDGE,"E19.8.0");var subQ2=makeQuery(id+"F2.imprint","INTERSECT",VERTEX,{"disambiguationData":[OD(0.0)],"derivedFrom":[subQ1,subQ0]});Q28=makeQuery(id+"F2.imprint","IMPRINT",FACE,{"disambiguationData":[TD([[makeQuery(id+"F2.imprint","IMPRINT",EDGE,{"disambiguationData":[TD([[subQ2,-1.0]])],"derivedFrom":subQ1}),-1.0]])]});}
            var Q29;
            {var subQ0=sQuery(id+"F2.wireOp",EDGE,"E35");var subQ1=sQuery(id+"F2.wireOp",EDGE,"E19.9.0");var subQ2=makeQuery(id+"F2.imprint","INTERSECT",VERTEX,{"disambiguationData":[OD(0.0)],"derivedFrom":[subQ1,subQ0]});Q29=makeQuery(id+"F2.imprint","IMPRINT",FACE,{"disambiguationData":[TD([[makeQuery(id+"F2.imprint","IMPRINT",EDGE,{"disambiguationData":[TD([[subQ2,-1.0]])],"derivedFrom":subQ1}),-1.0]])]});}
            var Q30;
            {var subQ0=sQuery(id+"F2.wireOp",EDGE,"E35");var subQ1=sQuery(id+"F2.wireOp",EDGE,"E19.10.0");var subQ2=makeQuery(id+"F2.imprint","INTERSECT",VERTEX,{"disambiguationData":[OD(0.0)],"derivedFrom":[subQ1,subQ0]});Q30=makeQuery(id+"F2.imprint","IMPRINT",FACE,{"disambiguationData":[TD([[makeQuery(id+"F2.imprint","IMPRINT",EDGE,{"disambiguationData":[TD([[subQ2,-1.0]])],"derivedFrom":subQ1}),-1.0]])]});}
            var Q31;
            {var subQ0=sQuery(id+"F2.wireOp",EDGE,"E35");var subQ1=makeQuery(id+"F2.imprint","IMPRINT",VERTEX,{"derivedFrom":subQ0});Q31=makeQuery(id+"F2.imprint","IMPRINT",FACE,{"disambiguationData":[TD([[makeQuery(id+"F2.imprint","IMPRINT",EDGE,{"disambiguationData":[TD([[subQ1,1.0]])],"derivedFrom":subQ0}),1.0]])]});}
            var Q32;
            {var subQ0=sQuery(id+"F2.wireOp",EDGE,"E35");var subQ1=sQuery(id+"F2.wireOp",EDGE,"E19.1.0");var subQ2=makeQuery(id+"F2.imprint","INTERSECT",VERTEX,{"disambiguationData":[OD(0.0)],"derivedFrom":[subQ1,subQ0]});Q32=makeQuery(id+"F2.imprint","IMPRINT",FACE,{"disambiguationData":[TD([[makeQuery(id+"F2.imprint","IMPRINT",EDGE,{"disambiguationData":[TD([[subQ2,1.0]])],"derivedFrom":subQ1}),1.0]])]});}
            var Q33;
            {var subQ0=sQuery(id+"F2.wireOp",EDGE,"E35");var subQ1=sQuery(id+"F2.wireOp",EDGE,"E19.2.0");var subQ2=makeQuery(id+"F2.imprint","INTERSECT",VERTEX,{"disambiguationData":[OD(0.0)],"derivedFrom":[subQ1,subQ0]});Q33=makeQuery(id+"F2.imprint","IMPRINT",FACE,{"disambiguationData":[TD([[makeQuery(id+"F2.imprint","IMPRINT",EDGE,{"disambiguationData":[TD([[subQ2,1.0]])],"derivedFrom":subQ1}),1.0]])]});}
            var Q34;
            {var subQ0=sQuery(id+"F2.wireOp",EDGE,"E35");var subQ1=sQuery(id+"F2.wireOp",EDGE,"E19.3.0");var subQ2=makeQuery(id+"F2.imprint","INTERSECT",VERTEX,{"disambiguationData":[OD(0.0)],"derivedFrom":[subQ1,subQ0]});Q34=makeQuery(id+"F2.imprint","IMPRINT",FACE,{"disambiguationData":[TD([[makeQuery(id+"F2.imprint","IMPRINT",EDGE,{"disambiguationData":[TD([[subQ2,1.0]])],"derivedFrom":subQ1}),1.0]])]});}
            var Q35;
            {var subQ0=sQuery(id+"F2.wireOp",EDGE,"E35");var subQ1=sQuery(id+"F2.wireOp",EDGE,"E19.5.0");var subQ2=makeQuery(id+"F2.imprint","INTERSECT",VERTEX,{"disambiguationData":[OD(0.0)],"derivedFrom":[subQ1,subQ0]});Q35=makeQuery(id+"F2.imprint","IMPRINT",FACE,{"disambiguationData":[TD([[makeQuery(id+"F2.imprint","IMPRINT",EDGE,{"disambiguationData":[TD([[subQ2,1.0]])],"derivedFrom":subQ1}),1.0]])]});}
            var Q36;
            {var subQ0=sQuery(id+"F2.wireOp",EDGE,"E35");var subQ1=sQuery(id+"F2.wireOp",EDGE,"E19.6.0");var subQ2=makeQuery(id+"F2.imprint","INTERSECT",VERTEX,{"disambiguationData":[OD(0.0)],"derivedFrom":[subQ1,subQ0]});Q36=makeQuery(id+"F2.imprint","IMPRINT",FACE,{"disambiguationData":[TD([[makeQuery(id+"F2.imprint","IMPRINT",EDGE,{"disambiguationData":[TD([[subQ2,-1.0]])],"derivedFrom":subQ1}),1.0]])]});}
            var Q37;
            {var subQ0=sQuery(id+"F2.wireOp",EDGE,"E35");var subQ1=sQuery(id+"F2.wireOp",EDGE,"E19.7.0");var subQ2=makeQuery(id+"F2.imprint","INTERSECT",VERTEX,{"disambiguationData":[OD(0.0)],"derivedFrom":[subQ1,subQ0]});Q37=makeQuery(id+"F2.imprint","IMPRINT",FACE,{"disambiguationData":[TD([[makeQuery(id+"F2.imprint","IMPRINT",EDGE,{"disambiguationData":[TD([[subQ2,-1.0]])],"derivedFrom":subQ1}),1.0]])]});}
            var Q38;
            {var subQ0=sQuery(id+"F2.wireOp",EDGE,"E35");var subQ1=sQuery(id+"F2.wireOp",EDGE,"E19.8.0");var subQ2=makeQuery(id+"F2.imprint","INTERSECT",VERTEX,{"disambiguationData":[OD(0.0)],"derivedFrom":[subQ1,subQ0]});Q38=makeQuery(id+"F2.imprint","IMPRINT",FACE,{"disambiguationData":[TD([[makeQuery(id+"F2.imprint","IMPRINT",EDGE,{"disambiguationData":[TD([[subQ2,-1.0]])],"derivedFrom":subQ1}),1.0]])]});}
            var Q39;
            {var subQ0=sQuery(id+"F2.wireOp",EDGE,"E35");var subQ1=sQuery(id+"F2.wireOp",EDGE,"E19.9.0");var subQ2=makeQuery(id+"F2.imprint","INTERSECT",VERTEX,{"disambiguationData":[OD(0.0)],"derivedFrom":[subQ1,subQ0]});Q39=makeQuery(id+"F2.imprint","IMPRINT",FACE,{"disambiguationData":[TD([[makeQuery(id+"F2.imprint","IMPRINT",EDGE,{"disambiguationData":[TD([[subQ2,-1.0]])],"derivedFrom":subQ1}),1.0]])]});}
            var Q40;
            {var subQ0=sQuery(id+"F2.wireOp",EDGE,"E35");var subQ1=sQuery(id+"F2.wireOp",EDGE,"E19.10.0");var subQ2=makeQuery(id+"F2.imprint","INTERSECT",VERTEX,{"disambiguationData":[OD(0.0)],"derivedFrom":[subQ1,subQ0]});Q40=makeQuery(id+"F2.imprint","IMPRINT",FACE,{"disambiguationData":[TD([[makeQuery(id+"F2.imprint","IMPRINT",EDGE,{"disambiguationData":[TD([[subQ2,-1.0]])],"derivedFrom":subQ1}),1.0]])]});}
            var Q41;
            {var subQ0=sQuery(id+"F2.wireOp",EDGE,"E35");var subQ1=sQuery(id+"F2.wireOp",EDGE,"E19.11.0");var subQ2=makeQuery(id+"F2.imprint","INTERSECT",VERTEX,{"disambiguationData":[OD(0.0)],"derivedFrom":[subQ1,subQ0]});Q41=makeQuery(id+"F2.imprint","IMPRINT",FACE,{"disambiguationData":[TD([[makeQuery(id+"F2.imprint","IMPRINT",EDGE,{"disambiguationData":[TD([[subQ2,-1.0]])],"derivedFrom":subQ1}),1.0]])]});}
            var Q42;
            {var subQ0=sQuery(id+"F2.wireOp",EDGE,"E35");var subQ1=sQuery(id+"F2.wireOp",EDGE,"E19.4.0");var subQ2=makeQuery(id+"F2.imprint","INTERSECT",VERTEX,{"disambiguationData":[OD(0.0)],"derivedFrom":[subQ1,subQ0]});Q42=makeQuery(id+"F2.imprint","IMPRINT",FACE,{"disambiguationData":[TD([[makeQuery(id+"F2.imprint","IMPRINT",EDGE,{"disambiguationData":[TD([[subQ2,1.0]])],"derivedFrom":subQ1}),1.0]])]});}
            var Q43;
            {var subQ0=sQuery(id+"F2.wireOp",EDGE,"E36");var subQ1=sQuery(id+"F2.wireOp",EDGE,"E19.3.0");var subQ2=makeQuery(id+"F2.imprint","INTERSECT",VERTEX,{"disambiguationData":[OD(0.0)],"derivedFrom":[subQ1,subQ0]});Q43=makeQuery(id+"F2.imprint","IMPRINT",FACE,{"disambiguationData":[TD([[makeQuery(id+"F2.imprint","IMPRINT",EDGE,{"disambiguationData":[TD([[subQ2,1.0]])],"derivedFrom":subQ1}),1.0]])]});}
            var Q44;
            Q44=makeQuery(id+"F2.imprint","IMPRINT",FACE,{"disambiguationData":[TD([[makeQuery(id+"F2.imprint","IMPRINT",EDGE,{"derivedFrom":sQuery(id+"F2.wireOp",EDGE,"E33.9.4")}),-1.0]])]});
            var Q45;
            Q45=makeQuery(id+"F2.imprint","IMPRINT",FACE,{"disambiguationData":[TD([[makeQuery(id+"F2.imprint","IMPRINT",EDGE,{"derivedFrom":sQuery(id+"F2.wireOp",EDGE,"E33.9.0")}),1.0]])]});
            var Q46;
            {var subQ0=sQuery(id+"F2.wireOp",EDGE,"E36");var subQ1=sQuery(id+"F2.wireOp",EDGE,"E19.2.0");var subQ2=makeQuery(id+"F2.imprint","INTERSECT",VERTEX,{"disambiguationData":[OD(0.0)],"derivedFrom":[subQ1,subQ0]});Q46=makeQuery(id+"F2.imprint","IMPRINT",FACE,{"disambiguationData":[TD([[makeQuery(id+"F2.imprint","IMPRINT",EDGE,{"disambiguationData":[TD([[subQ2,1.0]])],"derivedFrom":subQ1}),1.0]])]});}
            var Q47;
            Q47=makeQuery(id+"F2.imprint","IMPRINT",FACE,{"disambiguationData":[TD([[makeQuery(id+"F2.imprint","IMPRINT",EDGE,{"derivedFrom":sQuery(id+"F2.wireOp",EDGE,"E33.8.4")}),-1.0]])]});
            var Q48;
            Q48=makeQuery(id+"F2.imprint","IMPRINT",FACE,{"disambiguationData":[TD([[makeQuery(id+"F2.imprint","IMPRINT",EDGE,{"derivedFrom":sQuery(id+"F2.wireOp",EDGE,"E33.8.0")}),1.0]])]});
            var Q49;
            {var subQ0=sQuery(id+"F2.wireOp",EDGE,"E36");var subQ1=sQuery(id+"F2.wireOp",EDGE,"E19.1.0");var subQ2=makeQuery(id+"F2.imprint","INTERSECT",VERTEX,{"disambiguationData":[OD(0.0)],"derivedFrom":[subQ1,subQ0]});Q49=makeQuery(id+"F2.imprint","IMPRINT",FACE,{"disambiguationData":[TD([[makeQuery(id+"F2.imprint","IMPRINT",EDGE,{"disambiguationData":[TD([[subQ2,1.0]])],"derivedFrom":subQ1}),1.0]])]});}
            var Q50;
            Q50=makeQuery(id+"F2.imprint","IMPRINT",FACE,{"disambiguationData":[TD([[makeQuery(id+"F2.imprint","IMPRINT",EDGE,{"derivedFrom":sQuery(id+"F2.wireOp",EDGE,"E34.5.0")}),1.0]])]});
            var Q51;
            Q51=makeQuery(id+"F2.imprint","IMPRINT",FACE,{"disambiguationData":[TD([[makeQuery(id+"F2.imprint","IMPRINT",EDGE,{"derivedFrom":sQuery(id+"F2.wireOp",EDGE,"E33.7.4")}),-1.0]])]});
            var Q52;
            Q52=makeQuery(id+"F2.imprint","IMPRINT",FACE,{"disambiguationData":[TD([[makeQuery(id+"F2.imprint","IMPRINT",EDGE,{"derivedFrom":sQuery(id+"F2.wireOp",EDGE,"E33.7.0")}),1.0]])]});
            var Q53;
            {var subQ0=sQuery(id+"F2.wireOp",EDGE,"E36");var subQ4=makeQuery(id+"F2.imprint","IMPRINT",VERTEX,{"derivedFrom":subQ0});Q53=makeQuery(id+"F2.imprint","IMPRINT",FACE,{"disambiguationData":[TD([[makeQuery(id+"F2.imprint","IMPRINT",EDGE,{"disambiguationData":[TD([[subQ4,1.0]])],"derivedFrom":subQ0}),1.0]])]});}
            var Q54;
            Q54=makeQuery(id+"F2.imprint","IMPRINT",FACE,{"disambiguationData":[TD([[makeQuery(id+"F2.imprint","IMPRINT",EDGE,{"derivedFrom":sQuery(id+"F2.wireOp",EDGE,"E33.6.4")}),-1.0]])]});
            var Q55;
            Q55=makeQuery(id+"F2.imprint","IMPRINT",FACE,{"disambiguationData":[TD([[makeQuery(id+"F2.imprint","IMPRINT",EDGE,{"derivedFrom":sQuery(id+"F2.wireOp",EDGE,"E33.6.0")}),1.0]])]});
            var Q56;
            Q56=makeQuery(id+"F2.imprint","IMPRINT",FACE,{"disambiguationData":[TD([[makeQuery(id+"F2.imprint","IMPRINT",EDGE,{"derivedFrom":sQuery(id+"F2.wireOp",EDGE,"E34.4.0")}),1.0]])]});
            var Q57;
            Q57=makeQuery(id+"F2.imprint","IMPRINT",FACE,{"disambiguationData":[TD([[makeQuery(id+"F2.imprint","IMPRINT",EDGE,{"derivedFrom":sQuery(id+"F2.wireOp",EDGE,"E13")}),1.0]])]});
            var Q58;
            Q58=makeQuery(id+"F2.imprint","IMPRINT",FACE,{"disambiguationData":[TD([[makeQuery(id+"F2.imprint","IMPRINT",EDGE,{"derivedFrom":sQuery(id+"F2.wireOp",EDGE,"E23")}),1.0]])]});
            var Q59;
            {var subQ0=sQuery(id+"F2.wireOp",EDGE,"E36");var subQ1=sQuery(id+"F2.wireOp",EDGE,"E19.5.0");var subQ2=makeQuery(id+"F2.imprint","INTERSECT",VERTEX,{"disambiguationData":[OD(0.0)],"derivedFrom":[subQ1,subQ0]});Q59=makeQuery(id+"F2.imprint","IMPRINT",FACE,{"disambiguationData":[TD([[makeQuery(id+"F2.imprint","IMPRINT",EDGE,{"disambiguationData":[TD([[subQ2,1.0]])],"derivedFrom":subQ1}),1.0]])]});}
            var Q60;
            {var subQ0=sQuery(id+"F2.wireOp",EDGE,"E36");var subQ1=sQuery(id+"F2.wireOp",EDGE,"E19.6.0");var subQ2=makeQuery(id+"F2.imprint","INTERSECT",VERTEX,{"disambiguationData":[OD(0.0)],"derivedFrom":[subQ1,subQ0]});Q60=makeQuery(id+"F2.imprint","IMPRINT",FACE,{"disambiguationData":[TD([[makeQuery(id+"F2.imprint","IMPRINT",EDGE,{"disambiguationData":[TD([[subQ2,-1.0]])],"derivedFrom":subQ1}),1.0]])]});}
            var Q61;
            Q61=makeQuery(id+"F2.imprint","IMPRINT",FACE,{"disambiguationData":[TD([[makeQuery(id+"F2.imprint","IMPRINT",EDGE,{"derivedFrom":sQuery(id+"F2.wireOp",EDGE,"E29.MirrorCS")}),-1.0]])]});
            var Q62;
            Q62=makeQuery(id+"F2.imprint","IMPRINT",FACE,{"disambiguationData":[TD([[makeQuery(id+"F2.imprint","IMPRINT",EDGE,{"derivedFrom":sQuery(id+"F2.wireOp",EDGE,"E33.1.0")}),1.0]])]});
            var Q63;
            Q63=makeQuery(id+"F2.imprint","IMPRINT",FACE,{"disambiguationData":[TD([[makeQuery(id+"F2.imprint","IMPRINT",EDGE,{"derivedFrom":sQuery(id+"F2.wireOp",EDGE,"E33.1.4")}),-1.0]])]});
            var Q64;
            Q64=makeQuery(id+"F2.imprint","IMPRINT",FACE,{"disambiguationData":[TD([[makeQuery(id+"F2.imprint","IMPRINT",EDGE,{"derivedFrom":sQuery(id+"F2.wireOp",EDGE,"E34.2.0")}),1.0]])]});
            var Q65;
            Q65=makeQuery(id+"F2.imprint","IMPRINT",FACE,{"disambiguationData":[TD([[makeQuery(id+"F2.imprint","IMPRINT",EDGE,{"derivedFrom":sQuery(id+"F2.wireOp",EDGE,"E34.3.0")}),1.0]])]});
            var Q66;
            Q66=makeQuery(id+"F2.imprint","IMPRINT",FACE,{"disambiguationData":[TD([[makeQuery(id+"F2.imprint","IMPRINT",EDGE,{"derivedFrom":sQuery(id+"F2.wireOp",EDGE,"E33.2.0")}),1.0]])]});
            var Q67;
            Q67=makeQuery(id+"F2.imprint","IMPRINT",FACE,{"disambiguationData":[TD([[makeQuery(id+"F2.imprint","IMPRINT",EDGE,{"derivedFrom":sQuery(id+"F2.wireOp",EDGE,"E33.2.4")}),-1.0]])]});
            var Q68;
            {var subQ0=sQuery(id+"F2.wireOp",EDGE,"E36");var subQ1=sQuery(id+"F2.wireOp",EDGE,"E19.7.0");var subQ2=makeQuery(id+"F2.imprint","INTERSECT",VERTEX,{"disambiguationData":[OD(0.0)],"derivedFrom":[subQ1,subQ0]});Q68=makeQuery(id+"F2.imprint","IMPRINT",FACE,{"disambiguationData":[TD([[makeQuery(id+"F2.imprint","IMPRINT",EDGE,{"disambiguationData":[TD([[subQ2,-1.0]])],"derivedFrom":subQ1}),1.0]])]});}
            var Q69;
            Q69=makeQuery(id+"F2.imprint","IMPRINT",FACE,{"disambiguationData":[TD([[makeQuery(id+"F2.imprint","IMPRINT",EDGE,{"derivedFrom":sQuery(id+"F2.wireOp",EDGE,"E33.3.0")}),1.0]])]});
            var Q70;
            {var subQ0=sQuery(id+"F2.wireOp",EDGE,"E36");var subQ1=sQuery(id+"F2.wireOp",EDGE,"E19.8.0");var subQ2=makeQuery(id+"F2.imprint","INTERSECT",VERTEX,{"disambiguationData":[OD(0.0)],"derivedFrom":[subQ1,subQ0]});Q70=makeQuery(id+"F2.imprint","IMPRINT",FACE,{"disambiguationData":[TD([[makeQuery(id+"F2.imprint","IMPRINT",EDGE,{"disambiguationData":[TD([[subQ2,-1.0]])],"derivedFrom":subQ1}),1.0]])]});}
            var Q71;
            Q71=makeQuery(id+"F2.imprint","IMPRINT",FACE,{"disambiguationData":[TD([[makeQuery(id+"F2.imprint","IMPRINT",EDGE,{"derivedFrom":sQuery(id+"F2.wireOp",EDGE,"E33.3.4")}),-1.0]])]});
            var Q72;
            {var subQ0=sQuery(id+"F2.wireOp",EDGE,"E36");var subQ1=sQuery(id+"F2.wireOp",EDGE,"E19.9.0");var subQ2=makeQuery(id+"F2.imprint","INTERSECT",VERTEX,{"disambiguationData":[OD(0.0)],"derivedFrom":[subQ1,subQ0]});Q72=makeQuery(id+"F2.imprint","IMPRINT",FACE,{"disambiguationData":[TD([[makeQuery(id+"F2.imprint","IMPRINT",EDGE,{"disambiguationData":[TD([[subQ2,-1.0]])],"derivedFrom":subQ1}),1.0]])]});}
            var Q73;
            Q73=makeQuery(id+"F2.imprint","IMPRINT",FACE,{"disambiguationData":[TD([[makeQuery(id+"F2.imprint","IMPRINT",EDGE,{"derivedFrom":sQuery(id+"F2.wireOp",EDGE,"E33.4.0")}),1.0]])]});
            var Q74;
            Q74=makeQuery(id+"F2.imprint","IMPRINT",FACE,{"disambiguationData":[TD([[makeQuery(id+"F2.imprint","IMPRINT",EDGE,{"derivedFrom":sQuery(id+"F2.wireOp",EDGE,"E33.4.4")}),-1.0]])]});
            var Q75;
            {var subQ0=sQuery(id+"F2.wireOp",EDGE,"E36");var subQ1=sQuery(id+"F2.wireOp",EDGE,"E19.10.0");var subQ2=makeQuery(id+"F2.imprint","INTERSECT",VERTEX,{"disambiguationData":[OD(0.0)],"derivedFrom":[subQ1,subQ0]});Q75=makeQuery(id+"F2.imprint","IMPRINT",FACE,{"disambiguationData":[TD([[makeQuery(id+"F2.imprint","IMPRINT",EDGE,{"disambiguationData":[TD([[subQ2,-1.0]])],"derivedFrom":subQ1}),1.0]])]});}
            var Q76;
            Q76=makeQuery(id+"F2.imprint","IMPRINT",FACE,{"disambiguationData":[TD([[makeQuery(id+"F2.imprint","IMPRINT",EDGE,{"derivedFrom":sQuery(id+"F2.wireOp",EDGE,"E33.5.0")}),1.0]])]});
            var Q77;
            Q77=makeQuery(id+"F2.imprint","IMPRINT",FACE,{"disambiguationData":[TD([[makeQuery(id+"F2.imprint","IMPRINT",EDGE,{"derivedFrom":sQuery(id+"F2.wireOp",EDGE,"E33.5.4")}),-1.0]])]});
            var Q78;
            {var subQ0=sQuery(id+"F2.wireOp",EDGE,"E36");var subQ1=sQuery(id+"F2.wireOp",EDGE,"E19.11.0");var subQ2=makeQuery(id+"F2.imprint","INTERSECT",VERTEX,{"disambiguationData":[OD(0.0)],"derivedFrom":[subQ1,subQ0]});Q78=makeQuery(id+"F2.imprint","IMPRINT",FACE,{"disambiguationData":[TD([[makeQuery(id+"F2.imprint","IMPRINT",EDGE,{"disambiguationData":[TD([[subQ2,-1.0]])],"derivedFrom":subQ1}),1.0]])]});}
            var Q79;
            Q79=makeQuery(id+"F2.imprint","IMPRINT",FACE,{"disambiguationData":[TD([[makeQuery(id+"F2.imprint","IMPRINT",EDGE,{"derivedFrom":sQuery(id+"F2.wireOp",EDGE,"E38")}),1.0]])]});
            var Q80;
            Q80=makeQuery(id+"F2.imprint","IMPRINT",FACE,{"disambiguationData":[TD([[makeQuery(id+"F2.imprint","IMPRINT",EDGE,{"derivedFrom":sQuery(id+"F2.wireOp",EDGE,"E54.1.0")}),-1.0]])]});
            var Q81;
            Q81=makeQuery(id+"F2.imprint","IMPRINT",FACE,{"disambiguationData":[TD([[makeQuery(id+"F2.imprint","IMPRINT",EDGE,{"derivedFrom":sQuery(id+"F2.wireOp",EDGE,"E54.5.2")}),1.0]])]});
            var Q82;
            Q82=makeQuery(id+"F2.imprint","IMPRINT",FACE,{"disambiguationData":[TD([[makeQuery(id+"F2.imprint","IMPRINT",EDGE,{"derivedFrom":sQuery(id+"F2.wireOp",EDGE,"E53.MirrorC")}),-1.0]])]});
            var Q83;
            Q83=makeQuery(id+"F2.imprint","IMPRINT",FACE,{"disambiguationData":[TD([[makeQuery(id+"F2.imprint","IMPRINT",EDGE,{"derivedFrom":sQuery(id+"F2.wireOp",EDGE,"E52.MirrorC")}),-1.0]])]});
            var Q84;
            Q84=makeQuery(id+"F2.imprint","IMPRINT",FACE,{"disambiguationData":[TD([[makeQuery(id+"F2.imprint","IMPRINT",EDGE,{"derivedFrom":sQuery(id+"F2.wireOp",EDGE,"E54.1.1")}),-1.0]])]});
            var Q85;
            Q85=makeQuery(id+"F2.imprint","IMPRINT",FACE,{"disambiguationData":[TD([[makeQuery(id+"F2.imprint","IMPRINT",EDGE,{"derivedFrom":sQuery(id+"F2.wireOp",EDGE,"E54.5.3")}),1.0]])]});
            var Q86;
            Q86=makeQuery(id+"F2.imprint","IMPRINT",FACE,{"disambiguationData":[TD([[makeQuery(id+"F2.imprint","IMPRINT",EDGE,{"derivedFrom":sQuery(id+"F2.wireOp",EDGE,"E41.1.1")}),1.0]])]});
            var Q87;
            Q87=makeQuery(id+"F2.imprint","IMPRINT",FACE,{"disambiguationData":[TD([[makeQuery(id+"F2.imprint","IMPRINT",EDGE,{"derivedFrom":sQuery(id+"F2.wireOp",EDGE,"E41.11.1")}),1.0]])]});
            var Q88;
            Q88=makeQuery(id+"F2.imprint","IMPRINT",FACE,{"disambiguationData":[TD([[makeQuery(id+"F2.imprint","IMPRINT",EDGE,{"derivedFrom":sQuery(id+"F2.wireOp",EDGE,"E41.11.0")}),1.0]])]});
            var Q89;
            Q89=makeQuery(id+"F2.imprint","IMPRINT",FACE,{"disambiguationData":[TD([[makeQuery(id+"F2.imprint","IMPRINT",EDGE,{"derivedFrom":sQuery(id+"F2.wireOp",EDGE,"E41.1.0")}),1.0]])]});
            var Q90;
            Q90=makeQuery(id+"F2.imprint","IMPRINT",FACE,{"disambiguationData":[TD([[makeQuery(id+"F2.imprint","IMPRINT",EDGE,{"derivedFrom":sQuery(id+"F2.wireOp",EDGE,"E50")}),1.0]])]});
            var Q91;
            Q91=makeQuery(id+"F2.imprint","IMPRINT",FACE,{"disambiguationData":[TD([[makeQuery(id+"F2.imprint","IMPRINT",EDGE,{"derivedFrom":sQuery(id+"F2.wireOp",EDGE,"E51")}),1.0]])]});
            var Q92;
            Q92=makeQuery(id+"F2.imprint","IMPRINT",FACE,{"disambiguationData":[TD([[makeQuery(id+"F2.imprint","IMPRINT",EDGE,{"derivedFrom":sQuery(id+"F2.wireOp",EDGE,"E40")}),1.0]])]});
            var Q93;
            Q93=makeQuery(id+"F2.imprint","IMPRINT",FACE,{"disambiguationData":[TD([[makeQuery(id+"F2.imprint","IMPRINT",EDGE,{"derivedFrom":sQuery(id+"F2.wireOp",EDGE,"E54.4.2")}),1.0]])]});
            var Q94;
            Q94=makeQuery(id+"F2.imprint","IMPRINT",FACE,{"disambiguationData":[TD([[makeQuery(id+"F2.imprint","IMPRINT",EDGE,{"derivedFrom":sQuery(id+"F2.wireOp",EDGE,"E54.5.0")}),-1.0]])]});
            var Q95;
            Q95=makeQuery(id+"F2.imprint","IMPRINT",FACE,{"disambiguationData":[TD([[makeQuery(id+"F2.imprint","IMPRINT",EDGE,{"derivedFrom":sQuery(id+"F2.wireOp",EDGE,"E41.8.1")}),1.0]])]});
            var Q96;
            Q96=makeQuery(id+"F2.imprint","IMPRINT",FACE,{"disambiguationData":[TD([[makeQuery(id+"F2.imprint","IMPRINT",EDGE,{"derivedFrom":sQuery(id+"F2.wireOp",EDGE,"E54.5.1")}),-1.0]])]});
            var Q97;
            Q97=makeQuery(id+"F2.imprint","IMPRINT",FACE,{"disambiguationData":[TD([[makeQuery(id+"F2.imprint","IMPRINT",EDGE,{"derivedFrom":sQuery(id+"F2.wireOp",EDGE,"E41.9.1")}),1.0]])]});
            var Q98;
            Q98=makeQuery(id+"F2.imprint","IMPRINT",FACE,{"disambiguationData":[TD([[makeQuery(id+"F2.imprint","IMPRINT",EDGE,{"derivedFrom":sQuery(id+"F2.wireOp",EDGE,"E54.4.3")}),1.0]])]});
            var Q99;
            Q99=makeQuery(id+"F2.imprint","IMPRINT",FACE,{"disambiguationData":[TD([[makeQuery(id+"F2.imprint","IMPRINT",EDGE,{"derivedFrom":sQuery(id+"F2.wireOp",EDGE,"E41.8.0")}),1.0]])]});
            var Q100;
            Q100=makeQuery(id+"F2.imprint","IMPRINT",FACE,{"disambiguationData":[TD([[makeQuery(id+"F2.imprint","IMPRINT",EDGE,{"derivedFrom":sQuery(id+"F2.wireOp",EDGE,"E41.10.0")}),1.0]])]});
            var Q101;
            Q101=makeQuery(id+"F2.imprint","IMPRINT",FACE,{"disambiguationData":[TD([[makeQuery(id+"F2.imprint","IMPRINT",EDGE,{"derivedFrom":sQuery(id+"F2.wireOp",EDGE,"E41.10.1")}),1.0]])]});
            var Q102;
            Q102=makeQuery(id+"F2.imprint","IMPRINT",FACE,{"disambiguationData":[TD([[makeQuery(id+"F2.imprint","IMPRINT",EDGE,{"derivedFrom":sQuery(id+"F2.wireOp",EDGE,"E41.9.0")}),1.0]])]});
            var Q103;
            Q103=makeQuery(id+"F2.imprint","IMPRINT",FACE,{"disambiguationData":[TD([[makeQuery(id+"F2.imprint","IMPRINT",EDGE,{"derivedFrom":sQuery(id+"F2.wireOp",EDGE,"E41.7.0")}),1.0]])]});
            var Q104;
            Q104=makeQuery(id+"F2.imprint","IMPRINT",FACE,{"disambiguationData":[TD([[makeQuery(id+"F2.imprint","IMPRINT",EDGE,{"derivedFrom":sQuery(id+"F2.wireOp",EDGE,"E54.4.0")}),-1.0]])]});
            var Q105;
            Q105=makeQuery(id+"F2.imprint","IMPRINT",FACE,{"disambiguationData":[TD([[makeQuery(id+"F2.imprint","IMPRINT",EDGE,{"derivedFrom":sQuery(id+"F2.wireOp",EDGE,"E54.4.1")}),-1.0]])]});
            var Q106;
            Q106=makeQuery(id+"F2.imprint","IMPRINT",FACE,{"disambiguationData":[TD([[makeQuery(id+"F2.imprint","IMPRINT",EDGE,{"derivedFrom":sQuery(id+"F2.wireOp",EDGE,"E41.7.1")}),1.0]])]});
            var Q107;
            Q107=makeQuery(id+"F2.imprint","IMPRINT",FACE,{"disambiguationData":[TD([[makeQuery(id+"F2.imprint","IMPRINT",EDGE,{"derivedFrom":sQuery(id+"F2.wireOp",EDGE,"E54.3.3")}),1.0]])]});
            var Q108;
            Q108=makeQuery(id+"F2.imprint","IMPRINT",FACE,{"disambiguationData":[TD([[makeQuery(id+"F2.imprint","IMPRINT",EDGE,{"derivedFrom":sQuery(id+"F2.wireOp",EDGE,"E41.6.0")}),1.0]])]});
            var Q109;
            Q109=makeQuery(id+"F2.imprint","IMPRINT",FACE,{"disambiguationData":[TD([[makeQuery(id+"F2.imprint","IMPRINT",EDGE,{"derivedFrom":sQuery(id+"F2.wireOp",EDGE,"E41.5.1")}),1.0]])]});
            var Q110;
            Q110=makeQuery(id+"F2.imprint","IMPRINT",FACE,{"disambiguationData":[TD([[makeQuery(id+"F2.imprint","IMPRINT",EDGE,{"derivedFrom":sQuery(id+"F2.wireOp",EDGE,"E54.3.2")}),1.0]])]});
            var Q111;
            Q111=makeQuery(id+"F2.imprint","IMPRINT",FACE,{"disambiguationData":[TD([[makeQuery(id+"F2.imprint","IMPRINT",EDGE,{"derivedFrom":sQuery(id+"F2.wireOp",EDGE,"E41.5.0")}),1.0]])]});
            var Q112;
            Q112=makeQuery(id+"F2.imprint","IMPRINT",FACE,{"disambiguationData":[TD([[makeQuery(id+"F2.imprint","IMPRINT",EDGE,{"derivedFrom":sQuery(id+"F2.wireOp",EDGE,"E54.3.1")}),-1.0]])]});
            var Q113;
            Q113=makeQuery(id+"F2.imprint","IMPRINT",FACE,{"disambiguationData":[TD([[makeQuery(id+"F2.imprint","IMPRINT",EDGE,{"derivedFrom":sQuery(id+"F2.wireOp",EDGE,"E54.2.3")}),1.0]])]});
            var Q114;
            Q114=makeQuery(id+"F1.opRevolve","SWEPT_FACE",FACE,{"disambiguationData":[OSD([sQuery(id+"F0.wireOp",EDGE,"E2")])]});
            var Q115;
            Q115=makeQuery(id+"F2.imprint","IMPRINT",FACE,{"disambiguationData":[TD([[makeQuery(id+"F2.imprint","IMPRINT",EDGE,{"derivedFrom":sQuery(id+"F2.wireOp",EDGE,"E41.6.1")}),1.0]])]});
            var Q116;
            Q116=makeQuery(id+"F2.imprint","IMPRINT",FACE,{"disambiguationData":[TD([[makeQuery(id+"F2.imprint","IMPRINT",EDGE,{"derivedFrom":sQuery(id+"F2.wireOp",EDGE,"E54.3.0")}),-1.0]])]});
            var Q117;
            Q117=makeQuery(id+"F2.imprint","IMPRINT",FACE,{"disambiguationData":[TD([[makeQuery(id+"F2.imprint","IMPRINT",EDGE,{"derivedFrom":sQuery(id+"F2.wireOp",EDGE,"E54.1.2")}),1.0]])]});
            var Q118;
            Q118=makeQuery(id+"F2.imprint","IMPRINT",FACE,{"disambiguationData":[TD([[makeQuery(id+"F2.imprint","IMPRINT",EDGE,{"derivedFrom":sQuery(id+"F2.wireOp",EDGE,"E54.2.1")}),-1.0]])]});
            var Q119;
            Q119=makeQuery(id+"F2.imprint","IMPRINT",FACE,{"disambiguationData":[TD([[makeQuery(id+"F2.imprint","IMPRINT",EDGE,{"derivedFrom":sQuery(id+"F2.wireOp",EDGE,"E41.4.0")}),1.0]])]});
            var Q120;
            Q120=makeQuery(id+"F2.imprint","IMPRINT",FACE,{"disambiguationData":[TD([[makeQuery(id+"F2.imprint","IMPRINT",EDGE,{"derivedFrom":sQuery(id+"F2.wireOp",EDGE,"E41.3.1")}),1.0]])]});
            var Q121;
            Q121=makeQuery(id+"F2.imprint","IMPRINT",FACE,{"disambiguationData":[TD([[makeQuery(id+"F2.imprint","IMPRINT",EDGE,{"derivedFrom":sQuery(id+"F2.wireOp",EDGE,"E41.2.1")}),1.0]])]});
            var Q122;
            Q122=makeQuery(id+"F2.imprint","IMPRINT",FACE,{"disambiguationData":[TD([[makeQuery(id+"F2.imprint","IMPRINT",EDGE,{"derivedFrom":sQuery(id+"F2.wireOp",EDGE,"E54.2.0")}),-1.0]])]});
            var Q123;
            Q123=makeQuery(id+"F2.imprint","IMPRINT",FACE,{"disambiguationData":[TD([[makeQuery(id+"F2.imprint","IMPRINT",EDGE,{"derivedFrom":sQuery(id+"F2.wireOp",EDGE,"E41.3.0")}),1.0]])]});
            var Q124;
            Q124=makeQuery(id+"F2.imprint","IMPRINT",FACE,{"disambiguationData":[TD([[makeQuery(id+"F2.imprint","IMPRINT",EDGE,{"derivedFrom":sQuery(id+"F2.wireOp",EDGE,"E41.2.0")}),1.0]])]});
            var Q125;
            Q125=makeQuery(id+"F2.imprint","IMPRINT",FACE,{"disambiguationData":[TD([[makeQuery(id+"F2.imprint","IMPRINT",EDGE,{"derivedFrom":sQuery(id+"F2.wireOp",EDGE,"E41.4.1")}),1.0]])]});
            var Q126;
            Q126=makeQuery(id+"F2.imprint","IMPRINT",FACE,{"disambiguationData":[TD([[makeQuery(id+"F2.imprint","IMPRINT",EDGE,{"derivedFrom":sQuery(id+"F2.wireOp",EDGE,"E54.1.3")}),1.0]])]});
            var Q127;
            Q127=makeQuery(id+"F2.imprint","IMPRINT",FACE,{"disambiguationData":[TD([[makeQuery(id+"F2.imprint","IMPRINT",EDGE,{"derivedFrom":sQuery(id+"F2.wireOp",EDGE,"E54.2.2")}),1.0]])]});
            var Q128;
            {var subQ0=sQuery(id+"F2.wireOp",EDGE,"E57.1.0");Q128=makeQuery(id+"F2.imprint","IMPRINT",FACE,{"disambiguationData":[TD([[makeQuery(id+"F2.imprint","IMPRINT",EDGE,{"derivedFrom":subQ0}),1.0]])]});}
            var Q129;
            {var subQ0=sQuery(id+"F2.wireOp",EDGE,"E56.trimOffspring");Q129=makeQuery(id+"F2.imprint","IMPRINT",FACE,{"disambiguationData":[TD([[makeQuery(id+"F2.imprint","IMPRINT",EDGE,{"derivedFrom":subQ0}),1.0]])]});}
            var Q130;
            {var subQ0=sQuery(id+"F2.wireOp",EDGE,"E57.11.0");Q130=makeQuery(id+"F2.imprint","IMPRINT",FACE,{"disambiguationData":[TD([[makeQuery(id+"F2.imprint","IMPRINT",EDGE,{"derivedFrom":subQ0}),1.0]])]});}
            var Q131;
            {var subQ0=sQuery(id+"F2.wireOp",EDGE,"E57.10.0");Q131=makeQuery(id+"F2.imprint","IMPRINT",FACE,{"disambiguationData":[TD([[makeQuery(id+"F2.imprint","IMPRINT",EDGE,{"derivedFrom":subQ0}),1.0]])]});}
            var Q132;
            {var subQ0=sQuery(id+"F2.wireOp",EDGE,"E57.9.0");Q132=makeQuery(id+"F2.imprint","IMPRINT",FACE,{"disambiguationData":[TD([[makeQuery(id+"F2.imprint","IMPRINT",EDGE,{"derivedFrom":subQ0}),1.0]])]});}
            var Q133;
            {var subQ0=sQuery(id+"F2.wireOp",EDGE,"E57.8.0");Q133=makeQuery(id+"F2.imprint","IMPRINT",FACE,{"disambiguationData":[TD([[makeQuery(id+"F2.imprint","IMPRINT",EDGE,{"derivedFrom":subQ0}),1.0]])]});}
            var Q134;
            {var subQ0=sQuery(id+"F2.wireOp",EDGE,"E57.7.0");Q134=makeQuery(id+"F2.imprint","IMPRINT",FACE,{"disambiguationData":[TD([[makeQuery(id+"F2.imprint","IMPRINT",EDGE,{"derivedFrom":subQ0}),1.0]])]});}
            var Q135;
            {var subQ0=sQuery(id+"F2.wireOp",EDGE,"E57.6.0");Q135=makeQuery(id+"F2.imprint","IMPRINT",FACE,{"disambiguationData":[TD([[makeQuery(id+"F2.imprint","IMPRINT",EDGE,{"derivedFrom":subQ0}),1.0]])]});}
            var Q136;
            {var subQ0=sQuery(id+"F2.wireOp",EDGE,"E57.5.0");Q136=makeQuery(id+"F2.imprint","IMPRINT",FACE,{"disambiguationData":[TD([[makeQuery(id+"F2.imprint","IMPRINT",EDGE,{"derivedFrom":subQ0}),1.0]])]});}
            var Q137;
            {var subQ0=sQuery(id+"F2.wireOp",EDGE,"E57.4.0");Q137=makeQuery(id+"F2.imprint","IMPRINT",FACE,{"disambiguationData":[TD([[makeQuery(id+"F2.imprint","IMPRINT",EDGE,{"derivedFrom":subQ0}),1.0]])]});}
            var Q138;
            {var subQ0=sQuery(id+"F2.wireOp",EDGE,"E57.3.0");Q138=makeQuery(id+"F2.imprint","IMPRINT",FACE,{"disambiguationData":[TD([[makeQuery(id+"F2.imprint","IMPRINT",EDGE,{"derivedFrom":subQ0}),1.0]])]});}
            var Q139;
            {var subQ0=sQuery(id+"F2.wireOp",EDGE,"E57.2.0");Q139=makeQuery(id+"F2.imprint","IMPRINT",FACE,{"disambiguationData":[TD([[makeQuery(id+"F2.imprint","IMPRINT",EDGE,{"derivedFrom":subQ0}),1.0]])]});}
            var Q140;
            {var subQ1=sQuery(id+"F2.wireOp",EDGE,"E35");var subQ3=sQuery(id+"F2.wireOp",EDGE,"E19.6.0");var subQ4=makeQuery(id+"F2.imprint","INTERSECT",VERTEX,{"disambiguationData":[OD(1.0)],"derivedFrom":[subQ3,subQ1]});Q140=makeQuery(id+"F2.imprint","IMPRINT",FACE,{"disambiguationData":[TD([[makeQuery(id+"F2.imprint","IMPRINT",EDGE,{"disambiguationData":[TD([[subQ4,-1.0]])],"derivedFrom":subQ3}),-1.0]])]});}
            var Q141;
            {var subQ0=sQuery(id+"F2.wireOp",EDGE,"E36");var subQ1=sQuery(id+"F2.wireOp",EDGE,"E19.6.0");var subQ2=makeQuery(id+"F2.imprint","INTERSECT",VERTEX,{"disambiguationData":[OD(0.0)],"derivedFrom":[subQ1,subQ0]});Q141=makeQuery(id+"F2.imprint","IMPRINT",FACE,{"disambiguationData":[TD([[makeQuery(id+"F2.imprint","IMPRINT",EDGE,{"disambiguationData":[TD([[subQ2,1.0]])],"derivedFrom":subQ1}),1.0]])]});}
            extrude(context, id + "F3", {"entities" : qUnion([Q0, Q1, Q2, Q3, Q4, Q5, Q6, Q7, Q8, Q9, Q10, Q11, Q12, Q13, Q14, Q15, Q16, Q17, Q18, Q19, Q20, Q21, Q22, Q23, Q24, Q25, Q26, Q27, Q28, Q29, Q30, Q31, Q32, Q33, Q34, Q35, Q36, Q37, Q38, Q39, Q40, Q41, Q42, Q43, Q44, Q45, Q46, Q47, Q48, Q49, Q50, Q51, Q52, Q53, Q54, Q55, Q56, Q57, Q58, Q59, Q60, Q61, Q62, Q63, Q64, Q65, Q66, Q67, Q68, Q69, Q70, Q71, Q72, Q73, Q74, Q75, Q76, Q77, Q78, Q79, Q80, Q81, Q82, Q83, Q84, Q85, Q86, Q87, Q88, Q89, Q90, Q91, Q92, Q93, Q94, Q95, Q96, Q97, Q98, Q99, Q100, Q101, Q102, Q103, Q104, Q105, Q106, Q107, Q108, Q109, Q110, Q111, Q112, Q113, Q114, Q115, Q116, Q117, Q118, Q119, Q120, Q121, Q122, Q123, Q124, Q125, Q126, Q127, Q128, Q129, Q130, Q131, Q132, Q133, Q134, Q135, Q136, Q137, Q138, Q139, Q140, Q141]), "operationType" : NewBodyOperationType.REMOVE, "endBound" : BoundingType.THROUGH_ALL, "oppositeDirection" : true, "depth" : 25 * mm, "offsetDistance" : 25 * mm});
        }
        {
            var Q0;
            Q0=makeQuery(id+"F1.opRevolve","SWEPT_FACE",FACE,{"disambiguationData":[OSD([sQuery(id+"F0.wireOp",EDGE,"E0")])]});
            var sketch = newSketch(context, id + "F4", { "sketchPlane" : qUnion([Q0])});
            skCircle(sketch, "E58", {"center": v(0, 95) * mm, "radius": 6.88 * mm});
            skSolve(sketch);
        }
        {
            var Q0;
            Q0 = qSketchRegion(id + "F4", true);
            extrude(context, id + "F5", {"entities" : qUnion([Q0]), "oppositeDirection" : true, "depth" : 10.38 * mm - 1.57 * mm, "offsetDistance" : 25 * mm});
        }
        {
            var Q0;
            Q0=makeQuery(id+"F5.opExtrude","CAP_FACE",FACE,{"disambiguationData":[OSD([sQuery(id+"F4.wireOp",EDGE,"E58")])],"isStart":true});
            var sketch = newSketch(context, id + "F6", { "sketchPlane" : qUnion([Q0])});
            skCircle(sketch, "E59", {"center": v(0, 95) * mm, "radius": 10.5 * mm});
            skSolve(sketch);
        }
        {
            var Q0;
            Q0 = qSketchRegion(id + "F6", true);
            extrude(context, id + "F7", {"entities" : qUnion([Q0]), "operationType" : NewBodyOperationType.ADD, "depth" : 1.57 * mm, "offsetDistance" : 25 * mm});
        }
        {
            var Q0;
            Q0=makeQuery(id+"F7.opExtrude","CAP_FACE",FACE,{"disambiguationData":[OSD([sQuery(id+"F6.wireOp",EDGE,"E59")])],"isStart":false});
            var sketch = newSketch(context, id + "F8", { "sketchPlane" : qUnion([Q0])});
            skCircle(sketch, "E60", {"center": v(0, 95) * mm, "radius": 2.93 * mm});
            skSolve(sketch);
        }
        {
            var Q0;
            Q0=makeQuery(id+"F8.imprint","IMPRINT",FACE,{"disambiguationData":[TD([[makeQuery(id+"F8.imprint","IMPRINT",EDGE,{"derivedFrom":sQuery(id+"F8.wireOp",EDGE,"E60")}),1.0]])]});
            extrude(context, id + "F9", {"entities" : qUnion([Q0]), "operationType" : NewBodyOperationType.REMOVE, "endBound" : BoundingType.THROUGH_ALL, "oppositeDirection" : true, "depth" : 25 * mm, "offsetDistance" : 25 * mm});
        }
        {
            var Q0;
            Q0=makeQuery(id+"F7.opExtrude","CAP_FACE",FACE,{"disambiguationData":[OSD([sQuery(id+"F6.wireOp",EDGE,"E59")])],"isStart":false});
            var sketch = newSketch(context, id + "F10", { "sketchPlane" : qUnion([Q0])});
            skCircle(sketch, "E61", {"center": v(0, 95) * mm, "radius": 5 * mm});
            skSolve(sketch);
        }
        {
            var Q0;
            Q0 = qSketchRegion(id + "F10", true);
            extrude(context, id + "F11", {"entities" : qUnion([Q0]), "operationType" : NewBodyOperationType.REMOVE, "oppositeDirection" : true, "depth" : 5.5 * mm, "offsetDistance" : 25 * mm});
        }
        {
            var Q0;
            Q0=makeQuery(id+"F11.boolean.opBoolean","COPY",EDGE,{"derivedFrom":makeQuery(id+"F11.opExtrude","CAP_EDGE",EDGE,{"disambiguationData":[OSD([sQuery(id+"F10.wireOp",EDGE,"E61")])],"isStart":true})});
            var Q1;
            Q1=makeQuery(id+"F7.opExtrude","CAP_EDGE",EDGE,{"disambiguationData":[OSD([sQuery(id+"F6.wireOp",EDGE,"E59")])],"isStart":false});
            var Q2;
            Q2=makeQuery(id+"F11.boolean.opBoolean","COPY",EDGE,{"derivedFrom":makeQuery(id+"F11.opExtrude","CAP_EDGE",EDGE,{"disambiguationData":[OSD([sQuery(id+"F10.wireOp",EDGE,"E61")])],"isStart":false})});
            var Q3;
            Q3=makeQuery(id+"F11.boolean.opBoolean","INTERSECT",EDGE,{"derivedFrom":[makeQuery(id+"F9.boolean.opBoolean","COPY",FACE,{"derivedFrom":makeQuery(id+"F9.opExtrude","SWEPT_FACE",FACE,{"disambiguationData":[OSD([sQuery(id+"F8.wireOp",EDGE,"E60")])]})}),makeQuery(id+"F11.opExtrude","CAP_FACE",FACE,{"disambiguationData":[OSD([sQuery(id+"F10.wireOp",EDGE,"E61")])],"isStart":false})]});
            var Q4;
            Q4=makeQuery(id+"F5.opExtrude","CAP_EDGE",EDGE,{"disambiguationData":[OSD([sQuery(id+"F4.wireOp",EDGE,"E58")])],"isStart":false});
            chamfer(context, id + "F12", {"entities" : qUnion([Q0, Q1, Q2, Q3, Q4]), "width" : 0.5 * mm, "tangentPropagation" : true});
        }
        {
            var Q0;
            Q0=makeQuery(id+"F5.opExtrude","CAP_FACE",FACE,{"disambiguationData":[OSD([sQuery(id+"F4.wireOp",EDGE,"E58")])],"isStart":false});
            var sketch = newSketch(context, id + "F13", { "sketchPlane" : qUnion([Q0])});
            skLineSegment(sketch, "E62", {"start": v(0, 97.92) * mm, "end": v(0, 92.08) * mm});
            skSolve(sketch);
        }
        {
            var Q0;
            Q0=sQuery(id+"F13.wireOp",EDGE,"E62");
            cPlane(context, id + "F14", {"entities" : qUnion([Q0]), "cplaneType" : CPlaneType.LINE_ANGLE, "offset" : 25 * mm, "angle" : 90 * degree, "width" : 150 * mm, "height" : 150 * mm});
        }
        {
            var Q0;
            Q0=qCreatedBy(id+"F14.planeOp",FACE);
            var sketch = newSketch(context, id + "F15", { "sketchPlane" : qUnion([Q0])});
            skPoint(sketch, "E63.0", {"position": v(8.81, 95) * mm});
            skLineSegment(sketch, "E64", {"start": v(8.81, 95) * mm, "end": v(7.24, 95) * mm});
            skLineSegment(sketch, "E65", {"start": v(7.24, 95) * mm, "end": v(7.24, 99.4) * mm});
            skLineSegment(sketch, "E66.bottom", {"start": v(7.24, 99.4) * mm, "end": v(6.14, 99.4) * mm});
            skLineSegment(sketch, "E66.top", {"start": v(7.24, 102.17) * mm, "end": v(6.14, 102.17) * mm});
            skLineSegment(sketch, "E66.left", {"start": v(7.24, 99.4) * mm, "end": v(7.24, 102.17) * mm});
            skLineSegment(sketch, "E66.right", {"start": v(6.14, 99.4) * mm, "end": v(6.14, 102.17) * mm});
            skSolve(sketch);
        }
        {
            var Q0;
            Q0 = qSketchRegion(id + "F15", true);
            var Q1;
            Q1=sQuery(id+"F15.wireOp",EDGE,"E64");
            revolve(context, id + "F16", {"operationType" : NewBodyOperationType.REMOVE, "surfaceOperationType" : NewSurfaceOperationType.NEW, "entities" : qUnion([Q0]), "axis" : qUnion([Q1]), "revolveType" : RevolveType.FULL, "oppositeDirection" : true});
        }
        {
            var Q0;
            Q0=makeQuery(id+"F3.boolean.opBoolean","SPLIT",FACE,{"disambiguationData":[TD([makeQuery(id+"F1.opRevolve","SWEPT_FACE",FACE,{"disambiguationData":[OSD([sQuery(id+"F0.wireOp",EDGE,"E1")])]})])],"derivedFrom":makeQuery(id+"F1.opRevolve","SWEPT_FACE",FACE,{"disambiguationData":[OSD([sQuery(id+"F0.wireOp",EDGE,"E2")])]})});
            var sketch = newSketch(context, id + "F17", { "sketchPlane" : qUnion([Q0])});
            skCircle(sketch, "E67", {"center": v(0, 95) * mm, "radius": 7 * mm});
            skCircle(sketch, "E68", {"center": v(0, 95) * mm, "radius": 10 * mm});
            skSolve(sketch);
        }
        {
            var Q0;
            Q0 = qSketchRegion(id + "F17", true);
            extrude(context, id + "F18", {"entities" : qUnion([Q0]), "depth" : 1 * mm, "offsetDistance" : 25 * mm});
        }
        {
            var Q0;
            Q0=makeQuery(id+"F16.boolean.opBoolean","COPY",FACE,{"derivedFrom":makeQuery(id+"F16.opRevolve","SWEPT_FACE",FACE,{"disambiguationData":[OSD([sQuery(id+"F15.wireOp",EDGE,"E66.right")])]})});
            var sketch = newSketch(context, id + "F19", { "sketchPlane" : qUnion([Q0])});
            skArc(sketch, "E69", {"start": v(2.18, 103.9) * mm, "mid": v(-6.16, 88.22) * mm, "end": v(8.65, 98.02) * mm});
            skArc(sketch, "E70", {"start": v(0, 99.4) * mm, "mid": v(-1.54, 99.13) * mm, "end": v(-2.88, 98.34) * mm});
            skArc(sketch, "E71", {"start": v(-5.01, 100.46) * mm, "mid": v(-7.16, 96.95) * mm, "end": v(-7.09, 92.83) * mm});
            skLineSegment(sketch, "E72", {"start": v(3.45, 92.25) * mm, "end": v(5.58, 90.12) * mm});
            skLineSegment(sketch, "E73", {"start": v(-2.88, 98.34) * mm, "end": v(-5.01, 100.46) * mm});
            skLineSegment(sketch, "E74", {"start": v(-1.77, 90.96) * mm, "end": v(-1.77, 87.8) * mm});
            skLineSegment(sketch, "E75", {"start": v(-3.84, 92.83) * mm, "end": v(-7.09, 92.83) * mm});
            skArc(sketch, "E76.trimOffspring", {"start": v(3.45, 92.25) * mm, "mid": v(4.16, 93.55) * mm, "end": v(4.4, 95) * mm});
            skArc(sketch, "E77.trimOffspring", {"start": v(-3.84, 92.83) * mm, "mid": v(-2.95, 91.72) * mm, "end": v(-1.77, 90.96) * mm});
            skArc(sketch, "E78.trimOffspring", {"start": v(-1.77, 87.8) * mm, "mid": v(2.23, 87.93) * mm, "end": v(5.58, 90.12) * mm});
            skLineSegment(sketch, "E79", {"start": v(2.18, 103.9) * mm, "end": v(0, 99.4) * mm});
            skLineSegment(sketch, "E80", {"start": v(8.65, 98.02) * mm, "end": v(4.4, 95) * mm});
            skSolve(sketch);
        }
        {
            var Q0;
            Q0 = qSketchRegion(id + "F19", true);
            extrude(context, id + "F20", {"entities" : qUnion([Q0]), "depth" : 1.08 * mm, "offsetDistance" : 25 * mm});
        }
        {
            var Q0;
            Q0=makeQuery(id+"F5.opExtrude","SWEPT_BODY",BODY,{"disambiguationData":[OSD([sQuery(id+"F4.wireOp",EDGE,"E58")])]});
            var Q1;
            Q1=makeQuery(id+"F18.opExtrude","SWEPT_BODY",BODY,{"disambiguationData":[OSD([sQuery(id+"F17.wireOp",EDGE,"E67"),sQuery(id+"F17.wireOp",EDGE,"E68")])]});
            var Q2;
            Q2=makeQuery(id+"F20.opExtrude","SWEPT_BODY",BODY,{"disambiguationData":[OSD([sQuery(id+"F19.wireOp",EDGE,"E69"),sQuery(id+"F19.wireOp",EDGE,"E70"),sQuery(id+"F19.wireOp",EDGE,"E71"),sQuery(id+"F19.wireOp",EDGE,"E72"),sQuery(id+"F19.wireOp",EDGE,"E73"),sQuery(id+"F19.wireOp",EDGE,"E74"),sQuery(id+"F19.wireOp",EDGE,"E75"),sQuery(id+"F19.wireOp",EDGE,"E76.trimOffspring"),sQuery(id+"F19.wireOp",EDGE,"E77.trimOffspring"),sQuery(id+"F19.wireOp",EDGE,"E78.trimOffspring"),sQuery(id+"F19.wireOp",EDGE,"E79"),sQuery(id+"F19.wireOp",EDGE,"E80")])]});
            var Q3;
            Q3=makeQuery(id+"F3.boolean.opBoolean","INTERSECT",EDGE,{"derivedFrom":[makeQuery(id+"F1.opRevolve","SWEPT_FACE",FACE,{"disambiguationData":[OSD([sQuery(id+"F0.wireOp",EDGE,"E4")])]}),makeQuery(id+"F3.opExtrude","SWEPT_FACE",FACE,{"disambiguationData":[OSD([sQuery(id+"F2.wireOp",EDGE,"E13")])]})]});
            circularPattern(context, id + "F21", {"entities" : qUnion([Q0, Q1, Q2]), "axis" : qUnion([Q3]), "angle" : 360 * degree, "instanceCount" : 12, "equalSpace" : true, "computeTransformsWithoutBuiltin" : true});
        }
    });
